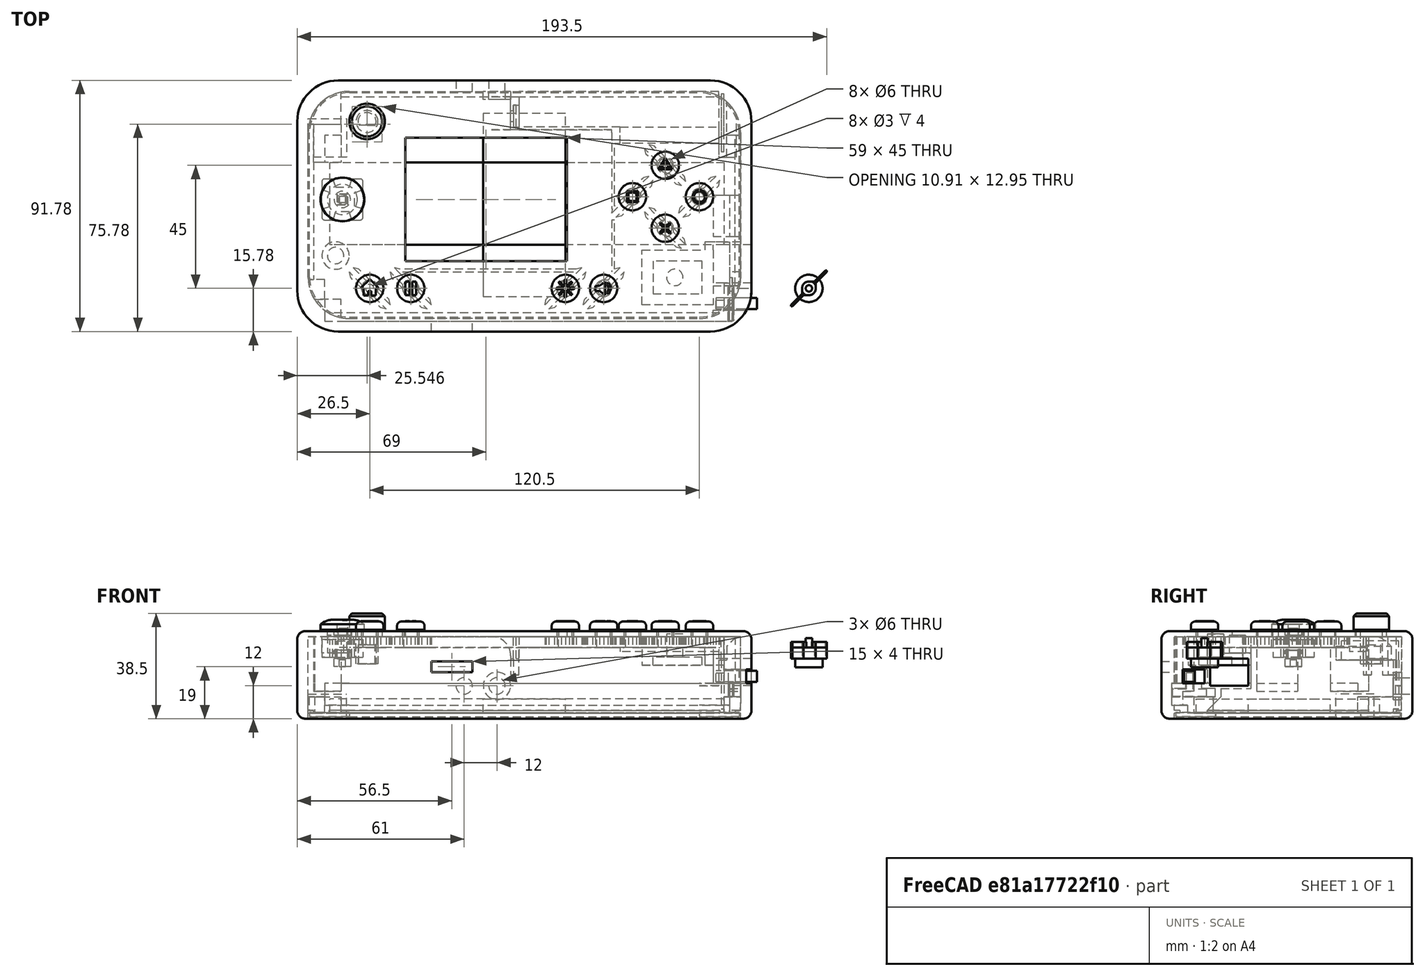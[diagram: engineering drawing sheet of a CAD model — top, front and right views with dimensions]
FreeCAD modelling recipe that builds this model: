
FCSTD DOCUMENT  (FreeCAD 0.18R4 (GitTag))
Label: Master
License: All rights reserved
LicenseURL: http://en.wikipedia.org/wiki/All_rights_reserved
objects: Sketcher::SketchObject×86, PartDesign::Pad×55, PartDesign::Pocket×27, PartDesign::Body×19, PartDesign::FeatureBase×8, PartDesign::Fillet×4, PartDesign::Chamfer×3, PartDesign::ShapeBinder×1, PartDesign::Revolution×1, PartDesign::PolarPattern×1
note: 288 computed .brp shape members not serialized (recipe doc carries the construction recipe); baked Part::Feature solids carry a one-line shape summary decoded from their .brp

FEATURE [Sketcher::SketchObject] Sketch
  MapMode = 5
  Support = -> [XY_Plane]
  sketch-geometry (17):
    g0: GeomPoint X=9e-16 Y=15 Z=0
    g1: GeomPoint X=0 Y=-72.9216 Z=0
    g2: LineSegment StartX=4 StartY=-70.7773 StartZ=0 EndX=140 EndY=-70.7773 EndZ=0
    g3: LineSegment StartX=4 StartY=21 StartZ=0 EndX=140 EndY=21 EndZ=0
    g4: LineSegment StartX=-11 StartY=6 StartZ=0 EndX=-11 EndY=-55.7773 EndZ=0
    g5: ArcOfCircle CenterX=140 CenterY=6 CenterZ=0 NormalX=0 NormalY=0 NormalZ=1 AngleXU=0 Radius=15 StartAngle=0 EndAngle=1.5708
    g6: ArcOfCircle CenterX=140 CenterY=-55.7773 CenterZ=0 NormalX=0 NormalY=0 NormalZ=1 AngleXU=0 Radius=15 StartAngle=4.71239 EndAngle=6.28319
    g7: LineSegment StartX=155 StartY=6 StartZ=0 EndX=155 EndY=-55.7773 EndZ=0
    g8: LineSegment [constr] StartX=140 StartY=21 StartZ=0 EndX=140 EndY=6 EndZ=0
    g9: LineSegment [constr] StartX=140 StartY=6 StartZ=0 EndX=140 EndY=-70.7773 EndZ=0
    g10: LineSegment [constr] StartX=140 StartY=-55.7773 StartZ=0 EndX=155 EndY=-55.7773 EndZ=0
    g11: LineSegment [constr] StartX=155 StartY=6 StartZ=0 EndX=140 EndY=6 EndZ=0
    g12: LineSegment [constr] StartX=4 StartY=21 StartZ=0 EndX=4 EndY=-70.7773 EndZ=0
    g13: ArcOfCircle CenterX=4 CenterY=-55.7773 CenterZ=0 NormalX=0 NormalY=0 NormalZ=1 AngleXU=0 Radius=15 StartAngle=3.14159 EndAngle=4.71239
    g14: LineSegment [constr] StartX=-11 StartY=-55.7773 StartZ=0 EndX=4 EndY=-55.7773 EndZ=0
    g15: LineSegment [constr] StartX=4 StartY=6 StartZ=0 EndX=-11 EndY=6 EndZ=0
    g16: ArcOfCircle CenterX=4 CenterY=6 CenterZ=0 NormalX=0 NormalY=0 NormalZ=1 AngleXU=0 Radius=15 StartAngle=1.5708 EndAngle=3.14159
  constraints (40):
    c: PointOnObject(g1,g-2)
    c: Horizontal(g2)
    c: Horizontal(g3)
    c: Vertical(g4)
    c: Coincident(g5,g3)
    c: Coincident(g6,g2)
    c: Coincident(g7,g5)
    c: Coincident(g7,g6)
    c: Vertical(g7)
    c: Coincident(g8,g3)
    c: Coincident(g8,g5)
    c: Vertical(g8)
    c: Coincident(g9,g5)
    c: Coincident(g9,g2)
    c: Vertical(g9)
    c: PointOnObject(g6,g9)
    c: Distance(g6,g2) = 15
    c: Coincident(g10,g6)
    c: Horizontal(g10)
    c: Coincident(g6,g10)
    c: Coincident(g11,g5)
    c: Coincident(g11,g5)
    c: Vertical(g12)
    c: PointOnObject(g13,g12)
    c: Coincident(g13,g12)
    c: Coincident(g14,g4)
    c: Coincident(g14,g13)
    c: Horizontal(g14)
    c: PointOnObject(g15,g12)
    c: Horizontal(g15)
    c: Coincident(g16,g15)
    c: PointOnObject(g15,g4)
    c: Coincident(g4,g16)
    c: Coincident(g3,g12)
    c: Coincident(g13,g4)
    c: Coincident(g3,g16)
    c: Coincident(g2,g12)
    c: Distance(g13,g2) = 15
    c: Distance(g3,g16) = 15
    c: Horizontal(g11)
FEATURE [PartDesign::Pad] Pad  label="Base"
  Length = 32
  Length2 = 100
  Profile = -> Sketch
  Type = 0
FEATURE [Sketcher::SketchObject] Sketch001
  MapMode = 5
  Placement = pos=(0,0,0) rot=(1,0,0;3.14159rad)
  Support = -> [Pad]
  sketch-geometry (12):
    g0: LineSegment StartX=8 StartY=-17 StartZ=0 EndX=136 EndY=-17 EndZ=0
    g1: LineSegment StartX=151 StartY=51 StartZ=0 EndX=151 EndY=-2 EndZ=0
    g2: LineSegment StartX=8 StartY=66 StartZ=0 EndX=136 EndY=66 EndZ=0
    g3: LineSegment StartX=-7 StartY=51 StartZ=0 EndX=-7 EndY=-2 EndZ=0
    g4: LineSegment [constr] StartX=-7 StartY=-17 StartZ=0 EndX=8 EndY=-2 EndZ=0
    g5: LineSegment [constr] StartX=-7 StartY=66 StartZ=0 EndX=8 EndY=51 EndZ=0
    g6: LineSegment [constr] StartX=151 StartY=66 StartZ=0 EndX=136 EndY=51 EndZ=0
    g7: LineSegment [constr] StartX=151 StartY=-17 StartZ=0 EndX=136 EndY=-2 EndZ=0
    g8: ArcOfCircle CenterX=8 CenterY=51 CenterZ=0 NormalX=0 NormalY=0 NormalZ=1 AngleXU=0 Radius=15 StartAngle=1.5708 EndAngle=3.14159
    g9: ArcOfCircle CenterX=136 CenterY=51 CenterZ=0 NormalX=0 NormalY=0 NormalZ=1 AngleXU=0 Radius=15 StartAngle=0 EndAngle=1.5708
    g10: ArcOfCircle CenterX=136 CenterY=-2 CenterZ=0 NormalX=0 NormalY=0 NormalZ=1 AngleXU=0 Radius=15 StartAngle=4.71239 EndAngle=6.28319
    g11: ArcOfCircle CenterX=8 CenterY=-2 CenterZ=0 NormalX=0 NormalY=0 NormalZ=1 AngleXU=0 Radius=15 StartAngle=3.14159 EndAngle=4.71239
  constraints (16):
    c: Horizontal(g0)
    c: Vertical(g1)
    c: Horizontal(g2)
    c: Vertical(g3)
    c: Coincident(g8,g5)
    c: Coincident(g9,g6)
    c: Coincident(g10,g7)
    c: Coincident(g11,g4)
    c: Coincident(g11,g3)
    c: Coincident(g11,g0)
    c: Coincident(g8,g2)
    c: Coincident(g8,g3)
    c: Coincident(g9,g1)
    c: Coincident(g9,g2)
    c: Coincident(g1,g10)
    c: Coincident(g0,g10)
FEATURE [Sketcher::SketchObject] Sketch002
  MapMode = 5
  Placement = pos=(0,0,32) rot=(0,0,1;0rad)
  Support = -> [Pad]
  sketch-geometry (30):
    g0: LineSegment [constr] StartX=0 StartY=0 StartZ=0 EndX=146 EndY=0 EndZ=0
    g1: LineSegment [constr] StartX=146 StartY=0 StartZ=0 EndX=146 EndY=-66 EndZ=0
    g2: LineSegment [constr] StartX=146 StartY=-66 StartZ=0 EndX=0 EndY=-66 EndZ=0
    g3: LineSegment [constr] StartX=0 StartY=-66 StartZ=0 EndX=0 EndY=0 EndZ=0
    g4: LineSegment [constr] StartX=15.5 StartY=-55 StartZ=0 EndX=101 EndY=-55 EndZ=0
    g5: GeomPoint X=30.5 Y=-55 Z=0
    g6: GeomPoint X=87 Y=-55 Z=0
    g7: LineSegment [constr] StartX=136 StartY=-21.5 StartZ=0 EndX=111.5 EndY=-21.5 EndZ=0
    g8: LineSegment [constr] StartX=123.5 StartY=-10 StartZ=0 EndX=123.5 EndY=-33 EndZ=0
    g9: LineSegment [constr] StartX=26 StartY=2.5 StartZ=0 EndX=94.5 EndY=2.5 EndZ=0
    g10: LineSegment [constr] StartX=94.5 StartY=2.5 StartZ=0 EndX=94.5 EndY=-47.5 EndZ=0
    g11: LineSegment [constr] StartX=94.5 StartY=-47.5 StartZ=0 EndX=26 EndY=-47.5 EndZ=0
    g12: LineSegment [constr] StartX=26 StartY=-47.5 StartZ=0 EndX=26 EndY=2.5 EndZ=0
    g13: GeomPoint X=5.5 Y=-22.5 Z=0
    g14: GeomPoint X=14.5 Y=4 Z=0
    g15: GeomPoint X=6 Y=-46 Z=0
    g16: Circle CenterX=15.5 CenterY=-55 CenterZ=0 NormalX=0 NormalY=0 NormalZ=1 AngleXU=0 Radius=3
    g17: Circle CenterX=30.5 CenterY=-55 CenterZ=0 NormalX=0 NormalY=0 NormalZ=1 AngleXU=0 Radius=3
    g18: Circle CenterX=87 CenterY=-55 CenterZ=0 NormalX=0 NormalY=0 NormalZ=1 AngleXU=0 Radius=3
    g19: Circle CenterX=101 CenterY=-55 CenterZ=0 NormalX=0 NormalY=0 NormalZ=1 AngleXU=0 Radius=3
    g20: Circle CenterX=111.5 CenterY=-21.5 CenterZ=0 NormalX=0 NormalY=0 NormalZ=1 AngleXU=0 Radius=3
    g21: Circle CenterX=136 CenterY=-21.5 CenterZ=0 NormalX=0 NormalY=0 NormalZ=1 AngleXU=0 Radius=3
    g22: Circle CenterX=123.5 CenterY=-33 CenterZ=0 NormalX=0 NormalY=0 NormalZ=1 AngleXU=0 Radius=3
    g23: Circle CenterX=123.5 CenterY=-10 CenterZ=0 NormalX=0 NormalY=0 NormalZ=1 AngleXU=0 Radius=3
    g24: LineSegment StartX=28.5 StartY=0 StartZ=0 EndX=87.5 EndY=0 EndZ=0
    g25: LineSegment StartX=87.5 StartY=0 StartZ=0 EndX=87.5 EndY=-45 EndZ=0
    g26: LineSegment StartX=87.5 StartY=-45 StartZ=0 EndX=28.5 EndY=-45 EndZ=0
    g27: LineSegment StartX=28.5 StartY=-45 StartZ=0 EndX=28.5 EndY=0 EndZ=0
    g28: Circle CenterX=5.5 CenterY=-22.5 CenterZ=0 NormalX=0 NormalY=0 NormalZ=1 AngleXU=0 Radius=5.5
    g29: Circle CenterX=14.5 CenterY=4 CenterZ=0 NormalX=0 NormalY=0 NormalZ=1 AngleXU=0 Radius=5.5
  constraints (63):
    c: Coincident(g0,g1)
    c: Coincident(g1,g2)
    c: Coincident(g2,g3)
    c: Coincident(g3,g0)
    c: Horizontal(g0)
    c: Horizontal(g2)
    c: Vertical(g1)
    c: Vertical(g3)
    c: Coincident(g0,g-1)
    c: Horizontal(g4)
    c: Distance(g3) = 66
    c: Distance(g0) = 146
    c: Distance(g4,g2) = 11
    c: Distance(g4,g3) = 15.5
    c: Distance(g4,g1) = 45
    c: PointOnObject(g5,g4)
    c: Distance(g4,g5) = 15
    c: PointOnObject(g6,g4)
    c: Distance(g6,g4) = 14
    c: Horizontal(g7)
    c: Vertical(g8)
    c: Distance(g7,g0) = 21.5
    c: Distance(g8,g1) = 22.5
    c: Distance(g8,g0) = 10
    c: Distance(g7,g1) = 10
    c: Distance(g8) = 23
    c: Distance(g7) = 24.5
    c: Coincident(g9,g10)
    c: Coincident(g10,g11)
    c: Coincident(g11,g12)
    c: Coincident(g12,g9)
    c: Horizontal(g9)
    c: Horizontal(g11)
    c: Vertical(g10)
    c: Vertical(g12)
    c: Distance(g12) = 50
    c: Distance(g11) = 68.5
    c: Distance(g9,g0) = 2.5
    c: Distance(g9,g3) = 26
    c: Distance(g13,g3) = 5.5
    c: Distance(g13,g0) = 22.5
    c: Distance(g14,g0) = 4
    c: Distance(g14,g3) = 14.5
    c: Distance(g15,g3) = 6
    c: Distance(g15,g2) = 20
    c: Coincident(g16,g4)
    c: Coincident(g17,g5)
    c: Coincident(g18,g6)
    c: Coincident(g19,g4)
    c: Coincident(g20,g7)
    c: Coincident(g22,g8)
    c: Coincident(g23,g8)
    c: Coincident(g24,g25)
    c: Coincident(g25,g26)
    c: Coincident(g26,g27)
    c: Coincident(g27,g24)
    c: Horizontal(g24)
    c: Horizontal(g26)
    c: Vertical(g25)
    c: Vertical(g27)
    c: Distance(g25,g10) = 7
    c: Coincident(g28,g13)
    c: Coincident(g29,g14)
FEATURE [Sketcher::SketchObject] Sketch003  label="Diagram"
  AttachmentOffset = pos=(0,0,-3) rot=(0,0,1;0rad)
  MapMode = 5
  Placement = pos=(0,0,29) rot=(0,0,1;0rad)
  Support = -> [Pad]
  sketch-geometry (34):
    g0: LineSegment StartX=0 StartY=0 StartZ=0 EndX=146 EndY=0 EndZ=0
    g1: LineSegment StartX=146 StartY=0 StartZ=0 EndX=146 EndY=-66 EndZ=0
    g2: LineSegment StartX=146 StartY=-66 StartZ=0 EndX=0 EndY=-66 EndZ=0
    g3: LineSegment StartX=0 StartY=-66 StartZ=0 EndX=0 EndY=0 EndZ=0
    g4: LineSegment [constr] StartX=15.5 StartY=-55 StartZ=0 EndX=101 EndY=-55 EndZ=0
    g5: GeomPoint X=30.5 Y=-55 Z=0
    g6: GeomPoint X=87 Y=-55 Z=0
    g7: LineSegment [constr] StartX=136 StartY=-21.5 StartZ=0 EndX=111.5 EndY=-21.5 EndZ=0
    g8: LineSegment [constr] StartX=123.5 StartY=-10 StartZ=0 EndX=123.5 EndY=-33 EndZ=0
    g9: LineSegment [constr] StartX=26 StartY=2.5 StartZ=0 EndX=94.5 EndY=2.5 EndZ=0
    g10: LineSegment [constr] StartX=94.5 StartY=2.5 StartZ=0 EndX=94.5 EndY=-47.5 EndZ=0
    g11: LineSegment [constr] StartX=94.5 StartY=-47.5 StartZ=0 EndX=26 EndY=-47.5 EndZ=0
    g12: LineSegment [constr] StartX=26 StartY=-47.5 StartZ=0 EndX=26 EndY=2.5 EndZ=0
    g13: GeomPoint X=5.5 Y=-22.5 Z=0
    g14: GeomPoint X=14.5 Y=4 Z=0
    g15: GeomPoint X=6 Y=-46 Z=0
    g16: Circle CenterX=15.5 CenterY=-55 CenterZ=0 NormalX=0 NormalY=0 NormalZ=1 AngleXU=0 Radius=3
    g17: Circle CenterX=30.5 CenterY=-55 CenterZ=0 NormalX=0 NormalY=0 NormalZ=1 AngleXU=0 Radius=3
    g18: Circle CenterX=87 CenterY=-55 CenterZ=0 NormalX=0 NormalY=0 NormalZ=1 AngleXU=0 Radius=3
    g19: Circle CenterX=101 CenterY=-55 CenterZ=0 NormalX=0 NormalY=0 NormalZ=1 AngleXU=0 Radius=3
    g20: Circle CenterX=111.5 CenterY=-21.5 CenterZ=0 NormalX=0 NormalY=0 NormalZ=1 AngleXU=0 Radius=3
    g21: Circle CenterX=136 CenterY=-21.5 CenterZ=0 NormalX=0 NormalY=0 NormalZ=1 AngleXU=0 Radius=3
    g22: Circle CenterX=123.5 CenterY=-33 CenterZ=0 NormalX=0 NormalY=0 NormalZ=1 AngleXU=0 Radius=3
    g23: Circle CenterX=123.5 CenterY=-10 CenterZ=0 NormalX=0 NormalY=0 NormalZ=1 AngleXU=0 Radius=3
    g24: LineSegment StartX=28.5 StartY=0 StartZ=0 EndX=87.5 EndY=0 EndZ=0
    g25: LineSegment StartX=87.5 StartY=0 StartZ=0 EndX=87.5 EndY=-45 EndZ=0
    g26: LineSegment StartX=87.5 StartY=-45 StartZ=0 EndX=28.5 EndY=-45 EndZ=0
    g27: LineSegment StartX=28.5 StartY=-45 StartZ=0 EndX=28.5 EndY=0 EndZ=0
    g28: Circle CenterX=5.5 CenterY=-22.5 CenterZ=0 NormalX=0 NormalY=0 NormalZ=1 AngleXU=0 Radius=3
    g29: Circle CenterX=14.5 CenterY=4 CenterZ=0 NormalX=0 NormalY=0 NormalZ=1 AngleXU=0 Radius=3
    g30: LineSegment StartX=142.166 StartY=-0.619292 StartZ=0 EndX=72.666 EndY=-0.619292 EndZ=0
    g31: LineSegment StartX=72.666 StartY=-0.619292 StartZ=0 EndX=72.666 EndY=17.3807 EndZ=0
    g32: LineSegment StartX=72.666 StartY=17.3807 StartZ=0 EndX=142.166 EndY=17.3807 EndZ=0
    g33: LineSegment StartX=142.166 StartY=17.3807 StartZ=0 EndX=142.166 EndY=-0.619292 EndZ=0
  constraints (72):
    c: Coincident(g0,g1)
    c: Coincident(g1,g2)
    c: Coincident(g2,g3)
    c: Coincident(g3,g0)
    c: Horizontal(g0)
    c: Horizontal(g2)
    c: Vertical(g1)
    c: Vertical(g3)
    c: Coincident(g0,g-1)
    c: Horizontal(g4)
    c: Distance(g3) = 66
    c: Distance(g0) = 146
    c: Distance(g4,g2) = 11
    c: Distance(g4,g3) = 15.5
    c: Distance(g4,g1) = 45
    c: PointOnObject(g5,g4)
    c: Distance(g4,g5) = 15
    c: PointOnObject(g6,g4)
    c: Distance(g6,g4) = 14
    c: Horizontal(g7)
    c: Vertical(g8)
    c: Distance(g7,g0) = 21.5
    c: Distance(g8,g1) = 22.5
    c: Distance(g8,g0) = 10
    c: Distance(g7,g1) = 10
    c: Distance(g8) = 23
    c: Distance(g7) = 24.5
    c: Coincident(g9,g10)
    c: Coincident(g10,g11)
    c: Coincident(g11,g12)
    c: Coincident(g12,g9)
    c: Horizontal(g9)
    c: Horizontal(g11)
    c: Vertical(g10)
    c: Vertical(g12)
    c: Distance(g12) = 50
    c: Distance(g11) = 68.5
    c: Distance(g9,g0) = 2.5
    c: Distance(g9,g3) = 26
    c: Distance(g13,g3) = 5.5
    c: Distance(g13,g0) = 22.5
    c: Distance(g14,g0) = 4
    c: Distance(g14,g3) = 14.5
    c: Distance(g15,g3) = 6
    c: Distance(g15,g2) = 20
    c: Coincident(g16,g4)
    c: Coincident(g17,g5)
    c: Coincident(g18,g6)
    c: Coincident(g19,g4)
    c: Coincident(g20,g7)
    c: Coincident(g22,g8)
    c: Coincident(g23,g8)
    c: Coincident(g24,g25)
    c: Coincident(g25,g26)
    c: Coincident(g26,g27)
    c: Coincident(g27,g24)
    c: Horizontal(g24)
    c: Horizontal(g26)
    c: Vertical(g25)
    c: Vertical(g27)
    c: Distance(g25,g10) = 7
    c: Coincident(g29,g14)
    c: Coincident(g30,g31)
    c: Coincident(g31,g32)
    c: Coincident(g32,g33)
    c: Coincident(g33,g30)
    c: Horizontal(g30)
    c: Horizontal(g32)
    c: Vertical(g31)
    c: Vertical(g33)
    c: Distance(g32) = 69.5
    c: Distance(g33) = 18
FEATURE [PartDesign::Pocket] Pocket  label="Input_holes"
  BaseFeature = -> Pad
  Length = 5
  Length2 = 100
  Profile = -> Sketch002
  Type = 0
FEATURE [PartDesign::Pocket] Pocket001  label="Cutout"
  BaseFeature = -> Pocket
  Length = 30
  Length2 = 100
  Profile = -> Sketch001
  Type = 0
FEATURE [Sketcher::SketchObject] Sketch004
  AttachmentOffset = pos=(0,0,17) rot=(0,0,1;0rad)
  MapMode = 5
  Placement = pos=(0,0,13) rot=(1,0,0;3.14159rad)
  Support = -> [Pocket001]
  sketch-geometry (4):
    g0: LineSegment StartX=147 StartY=58 StartZ=0 EndX=-1 EndY=58 EndZ=0
    g1: LineSegment StartX=-1 StartY=58 StartZ=0 EndX=-1 EndY=67 EndZ=0
    g2: LineSegment StartX=-1 StartY=67 StartZ=0 EndX=147 EndY=67 EndZ=0
    g3: LineSegment StartX=147 StartY=67 StartZ=0 EndX=147 EndY=58 EndZ=0
  constraints (8):
    c: Coincident(g0,g1)
    c: Coincident(g1,g2)
    c: Coincident(g2,g3)
    c: Coincident(g3,g0)
    c: Horizontal(g0)
    c: Horizontal(g2)
    c: Vertical(g1)
    c: Vertical(g3)
FEATURE [PartDesign::Pocket] Pocket002  label="PCB rack"
  BaseFeature = -> Pocket001
  Length = 8
  Length2 = 100
  Profile = -> Sketch004
  Reversed = true
  Type = 0
FEATURE [Sketcher::SketchObject] Sketch005
  MapMode = 5
  Placement = pos=(0,0,30) rot=(1,0,0;3.14159rad)
  Support = -> [Pocket002]
  sketch-geometry (16):
    g0: LineSegment StartX=5 StartY=9 StartZ=0 EndX=-5 EndY=9 EndZ=0
    g1: LineSegment StartX=-5 StartY=9 StartZ=0 EndX=-5 EndY=-5 EndZ=0
    g2: LineSegment StartX=-5 StartY=-5 StartZ=0 EndX=5 EndY=-5 EndZ=0
    g3: LineSegment StartX=5 StartY=-5 StartZ=0 EndX=5 EndY=9 EndZ=0
    g4: LineSegment StartX=5 StartY=59 StartZ=0 EndX=-5 EndY=59 EndZ=0
    g5: LineSegment StartX=-5 StartY=59 StartZ=0 EndX=-5 EndY=67 EndZ=0
    g6: LineSegment StartX=-5 StartY=67 StartZ=0 EndX=5 EndY=67 EndZ=0
    g7: LineSegment StartX=5 StartY=67 StartZ=0 EndX=5 EndY=59 EndZ=0
    g8: LineSegment StartX=141 StartY=63 StartZ=0 EndX=150 EndY=63 EndZ=0
    g9: LineSegment StartX=150 StartY=63 StartZ=0 EndX=150 EndY=66 EndZ=0
    g10: LineSegment StartX=150 StartY=66 StartZ=0 EndX=141 EndY=66 EndZ=0
    g11: LineSegment StartX=141 StartY=66 StartZ=0 EndX=141 EndY=63 EndZ=0
    g12: LineSegment StartX=149 StartY=21 StartZ=0 EndX=141 EndY=21 EndZ=0
    g13: LineSegment StartX=141 StartY=21 StartZ=0 EndX=141 EndY=36 EndZ=0
    g14: LineSegment StartX=141 StartY=36 StartZ=0 EndX=149 EndY=36 EndZ=0
    g15: LineSegment StartX=149 StartY=36 StartZ=0 EndX=149 EndY=21 EndZ=0
  constraints (32):
    c: Coincident(g0,g1)
    c: Coincident(g1,g2)
    c: Coincident(g2,g3)
    c: Coincident(g3,g0)
    c: Horizontal(g0)
    c: Horizontal(g2)
    c: Vertical(g1)
    c: Vertical(g3)
    c: Coincident(g4,g5)
    c: Coincident(g5,g6)
    c: Coincident(g6,g7)
    c: Coincident(g7,g4)
    c: Horizontal(g4)
    c: Horizontal(g6)
    c: Vertical(g5)
    c: Vertical(g7)
    c: Coincident(g8,g9)
    c: Coincident(g9,g10)
    c: Coincident(g10,g11)
    c: Coincident(g11,g8)
    c: Horizontal(g8)
    c: Horizontal(g10)
    c: Vertical(g9)
    c: Vertical(g11)
    c: Coincident(g12,g13)
    c: Coincident(g13,g14)
    c: Coincident(g14,g15)
    c: Coincident(g15,g12)
    c: Horizontal(g12)
    c: Horizontal(g14)
    c: Vertical(g13)
    c: Vertical(g15)
FEATURE [PartDesign::Pad] Pad001  label="PCB holders"
  BaseFeature = -> Pocket002
  Length = 17
  Length2 = 100
  Profile = -> Sketch005
  Type = 0
FEATURE [Sketcher::SketchObject] Sketch007
  MapMode = 5
  Placement = pos=(0,0,13) rot=(1,0,0;3.14159rad)
  Support = -> [Pad001]
  sketch-geometry (14):
    g0: LineSegment StartX=5 StartY=-5 StartZ=0 EndX=5 EndY=-1 EndZ=0
    g1: LineSegment StartX=5 StartY=-1 StartZ=0 EndX=-1 EndY=-1 EndZ=0
    g2: LineSegment StartX=-1 StartY=-1 StartZ=0 EndX=-1 EndY=9 EndZ=0
    g3: LineSegment StartX=-1 StartY=9 StartZ=0 EndX=-5 EndY=9 EndZ=0
    g4: LineSegment StartX=-5 StartY=9 StartZ=0 EndX=-5 EndY=-5 EndZ=0
    g5: LineSegment StartX=-5 StartY=-5 StartZ=0 EndX=5 EndY=-5 EndZ=0
    g6: LineSegment StartX=-1 StartY=59 StartZ=0 EndX=-1 EndY=64 EndZ=0
    g7: LineSegment StartX=-1 StartY=64 StartZ=0 EndX=-5 EndY=64 EndZ=0
    g8: LineSegment StartX=-5 StartY=64 StartZ=0 EndX=-5 EndY=59 EndZ=0
    g9: LineSegment StartX=-5 StartY=59 StartZ=0 EndX=-1 EndY=59 EndZ=0
    g10: LineSegment StartX=147 StartY=36 StartZ=0 EndX=151 EndY=36 EndZ=0
    g11: LineSegment StartX=151 StartY=36 StartZ=0 EndX=151 EndY=21 EndZ=0
    g12: LineSegment StartX=151 StartY=21 StartZ=0 EndX=147 EndY=21 EndZ=0
    g13: LineSegment StartX=147 StartY=21 StartZ=0 EndX=147 EndY=36 EndZ=0
  constraints (28):
    c: Vertical(g0)
    c: Coincident(g0,g1)
    c: Horizontal(g1)
    c: Coincident(g1,g2)
    c: Vertical(g2)
    c: Coincident(g2,g3)
    c: Horizontal(g3)
    c: Coincident(g3,g4)
    c: Vertical(g4)
    c: Coincident(g4,g5)
    c: Coincident(g5,g0)
    c: Horizontal(g5)
    c: Vertical(g6)
    c: Coincident(g6,g7)
    c: Horizontal(g7)
    c: Coincident(g7,g8)
    c: Vertical(g8)
    c: Coincident(g8,g9)
    c: Coincident(g9,g6)
    c: Horizontal(g9)
    c: Coincident(g10,g11)
    c: Coincident(g11,g12)
    c: Coincident(g12,g13)
    c: Coincident(g13,g10)
    c: Horizontal(g10)
    c: Horizontal(g12)
    c: Vertical(g11)
    c: Vertical(g13)
FEATURE [PartDesign::Pad] Pad002  label="PCB holder rims"
  BaseFeature = -> Pad001
  Length = 3
  Length2 = 100
  Profile = -> Sketch007
  Type = 0
FEATURE [Sketcher::SketchObject] Sketch008
  MapMode = 5
  Placement = pos=(0,0,30) rot=(1,0,0;3.14159rad)
  Support = -> [Pad002]
  sketch-geometry (4):
    g0: LineSegment StartX=70 StartY=-15 StartZ=0 EndX=143 EndY=-15 EndZ=0
    g1: LineSegment StartX=143 StartY=-15 StartZ=0 EndX=143 EndY=-17 EndZ=0
    g2: LineSegment StartX=143 StartY=-17 StartZ=0 EndX=70 EndY=-17 EndZ=0
    g3: LineSegment StartX=70 StartY=-17 StartZ=0 EndX=70 EndY=-15 EndZ=0
  constraints (8):
    c: Coincident(g0,g1)
    c: Coincident(g1,g2)
    c: Coincident(g2,g3)
    c: Coincident(g3,g0)
    c: Horizontal(g0)
    c: Horizontal(g2)
    c: Vertical(g1)
    c: Vertical(g3)
FEATURE [PartDesign::Pocket] Pocket003  label="Battery cutout"
  BaseFeature = -> Pad002
  Length = 18
  Length2 = 100
  Profile = -> Sketch008
  Reversed = true
  Type = 0
FEATURE [Sketcher::SketchObject] Sketch009
  MapMode = 5
  Placement = pos=(0,0,30) rot=(1,0,0;3.14159rad)
  Support = -> [Pocket003]
  sketch-geometry (4):
    g0: LineSegment StartX=143 StartY=7 StartZ=0 EndX=146 EndY=7 EndZ=0
    g1: LineSegment StartX=146 StartY=7 StartZ=0 EndX=146 EndY=-16 EndZ=0
    g2: LineSegment StartX=146 StartY=-16 StartZ=0 EndX=143 EndY=-16 EndZ=0
    g3: LineSegment StartX=143 StartY=-16 StartZ=0 EndX=143 EndY=7 EndZ=0
  constraints (8):
    c: Coincident(g0,g1)
    c: Coincident(g1,g2)
    c: Coincident(g2,g3)
    c: Coincident(g3,g0)
    c: Horizontal(g0)
    c: Horizontal(g2)
    c: Vertical(g1)
    c: Vertical(g3)
FEATURE [PartDesign::Pad] Pad003  label="Battery holder +"
  BaseFeature = -> Pocket003
  Length = 8.5
  Length2 = 100
  Profile = -> Sketch009
  Type = 0
FEATURE [Sketcher::SketchObject] Sketch010
  MapMode = 5
  Placement = pos=(0,0,21.5) rot=(1,0,0;3.14159rad)
  Support = -> [Pad003]
  sketch-geometry (4):
    g0: LineSegment StartX=144 StartY=5 StartZ=0 EndX=145 EndY=5 EndZ=0
    g1: LineSegment StartX=145 StartY=5 StartZ=0 EndX=145 EndY=-16 EndZ=0
    g2: LineSegment StartX=145 StartY=-16 StartZ=0 EndX=144 EndY=-16 EndZ=0
    g3: LineSegment StartX=144 StartY=-16 StartZ=0 EndX=144 EndY=5 EndZ=0
  constraints (8):
    c: Coincident(g0,g1)
    c: Coincident(g1,g2)
    c: Coincident(g2,g3)
    c: Coincident(g3,g0)
    c: Horizontal(g0)
    c: Horizontal(g2)
    c: Vertical(g1)
    c: Vertical(g3)
FEATURE [PartDesign::Pocket] Pocket004  label="Battery holder (+) cutout"
  BaseFeature = -> Pad003
  Length = 7
  Length2 = 100
  Profile = -> Sketch010
  Type = 0
FEATURE [Sketcher::SketchObject] Sketch011
  MapMode = 5
  Placement = pos=(0,0,21.5) rot=(1,0,0;3.14159rad)
  Support = -> [Pad003]
  sketch-geometry (4):
    g0: LineSegment StartX=144 StartY=5 StartZ=0 EndX=145 EndY=5 EndZ=0
    g1: LineSegment StartX=145 StartY=5 StartZ=0 EndX=145 EndY=-16 EndZ=0
    g2: LineSegment StartX=145 StartY=-16 StartZ=0 EndX=144 EndY=-16 EndZ=0
    g3: LineSegment StartX=144 StartY=-16 StartZ=0 EndX=144 EndY=5 EndZ=0
  constraints (8):
    c: Coincident(g0,g1)
    c: Coincident(g1,g2)
    c: Coincident(g2,g3)
    c: Coincident(g3,g0)
    c: Horizontal(g0)
    c: Horizontal(g2)
    c: Vertical(g1)
    c: Vertical(g3)
FEATURE [PartDesign::Pocket] Pocket005  label="Battery holder (+) up cutout"
  BaseFeature = -> Pocket004
  Length = 18
  Length2 = 100
  Profile = -> Sketch011
  Reversed = true
  Type = 0
FEATURE [Sketcher::SketchObject] Sketch012
  MapMode = 5
  Placement = pos=(0,0,30) rot=(1,0,0;3.14159rad)
  Support = -> [Pocket005]
  sketch-geometry (4):
    g0: LineSegment StartX=70 StartY=-2 StartZ=0 EndX=67 EndY=-2 EndZ=0
    g1: LineSegment StartX=67 StartY=-2 StartZ=0 EndX=67 EndY=-15 EndZ=0
    g2: LineSegment StartX=67 StartY=-15 StartZ=0 EndX=70 EndY=-15 EndZ=0
    g3: LineSegment StartX=70 StartY=-15 StartZ=0 EndX=70 EndY=-2 EndZ=0
  constraints (8):
    c: Coincident(g0,g1)
    c: Coincident(g1,g2)
    c: Coincident(g2,g3)
    c: Coincident(g3,g0)
    c: Horizontal(g0)
    c: Horizontal(g2)
    c: Vertical(g1)
    c: Vertical(g3)
FEATURE [PartDesign::Pad] Pad004  label="Battery holder (-)"
  BaseFeature = -> Pocket005
  Length = 8
  Length2 = 100
  Profile = -> Sketch012
  Type = 0
FEATURE [Sketcher::SketchObject] Sketch013
  MapMode = 5
  Placement = pos=(0,0,22) rot=(1,0,0;3.14159rad)
  Support = -> [Pad004]
  sketch-geometry (4):
    g0: LineSegment StartX=69 StartY=-12 StartZ=0 EndX=68 EndY=-12 EndZ=0
    g1: LineSegment StartX=68 StartY=-12 StartZ=0 EndX=68 EndY=-4 EndZ=0
    g2: LineSegment StartX=68 StartY=-4 StartZ=0 EndX=69 EndY=-4 EndZ=0
    g3: LineSegment StartX=69 StartY=-4 StartZ=0 EndX=69 EndY=-12 EndZ=0
  constraints (8):
    c: Coincident(g0,g1)
    c: Coincident(g1,g2)
    c: Coincident(g2,g3)
    c: Coincident(g3,g0)
    c: Horizontal(g0)
    c: Horizontal(g2)
    c: Vertical(g1)
    c: Vertical(g3)
FEATURE [PartDesign::Pocket] Pocket006  label="Battery holder (-) cutout"
  BaseFeature = -> Pad004
  Length = 8
  Length2 = 100
  Profile = -> Sketch013
  Type = 0
FEATURE [Sketcher::SketchObject] Sketch014
  MapMode = 5
  Placement = pos=(0,0,30) rot=(1,0,0;3.14159rad)
  Support = -> [Pocket006]
  sketch-geometry (143):
    g0: LineSegment [constr] StartX=58.75 StartY=60 StartZ=0 EndX=58.75 EndY=48.75 EndZ=0
    g1: LineSegment [constr] StartX=15.5 StartY=55 StartZ=0 EndX=72 EndY=55 EndZ=0
    g2: LineSegment [constr] StartX=101 StartY=55 StartZ=0 EndX=94.5 EndY=61.5 EndZ=0
    g3: LineSegment [constr] StartX=101 StartY=55 StartZ=0 EndX=107.5 EndY=48.5 EndZ=0
    g4: LineSegment [constr] StartX=136 StartY=21.5 StartZ=0 EndX=129.5 EndY=28 EndZ=0
    g5: LineSegment [constr] StartX=136 StartY=21.5 StartZ=0 EndX=142.5 EndY=15 EndZ=0
    g6: LineSegment [constr] StartX=123.5 StartY=10 StartZ=0 EndX=117 EndY=3.5 EndZ=0
    g7: LineSegment [constr] StartX=123.5 StartY=10 StartZ=0 EndX=130 EndY=16.5 EndZ=0
    g8: LineSegment [constr] StartX=111.5 StartY=21.5 StartZ=0 EndX=118 EndY=15 EndZ=0
    g9: LineSegment [constr] StartX=111.5 StartY=21.5 StartZ=0 EndX=105 EndY=28 EndZ=0
    g10: LineSegment StartX=123.5 StartY=7 StartZ=0 EndX=119.5 EndY=3 EndZ=0
    g11: LineSegment StartX=117.5 StartY=2.5 StartZ=0 EndX=122 EndY=7 EndZ=0
    g12: LineSegment StartX=122 StartY=7 StartZ=0 EndX=123.5 EndY=7 EndZ=0
    g13: LineSegment StartX=120.5 StartY=8.5 StartZ=0 EndX=120.5 EndY=10 EndZ=0
    g14: LineSegment StartX=120.5 StartY=8.5 StartZ=0 EndX=116 EndY=4 EndZ=0
    g15: LineSegment StartX=120.5 StartY=10 StartZ=0 EndX=116.5 EndY=6 EndZ=0
    g16: LineSegment StartX=126.5 StartY=10 StartZ=0 EndX=130.5 EndY=14 EndZ=0
    g17: LineSegment StartX=131 StartY=16 StartZ=0 EndX=126.5 EndY=11.5 EndZ=0
    g18: LineSegment StartX=126.5 StartY=11.5 StartZ=0 EndX=126.5 EndY=10 EndZ=0
    g19: LineSegment StartX=123.5 StartY=13 StartZ=0 EndX=125 EndY=13 EndZ=0
    g20: LineSegment StartX=125 StartY=13 StartZ=0 EndX=129.5 EndY=17.5 EndZ=0
    g21: LineSegment StartX=123.5 StartY=13 StartZ=0 EndX=127.5 EndY=17 EndZ=0
    g22: LineSegment StartX=119.5 StartY=3 StartZ=0 EndX=117.5 EndY=2.5 EndZ=0
    g23: LineSegment StartX=116.5 StartY=6 StartZ=0 EndX=116 EndY=4 EndZ=0
    g24: LineSegment StartX=129.5 StartY=17.5 StartZ=0 EndX=127.5 EndY=17 EndZ=0
    g25: LineSegment StartX=131 StartY=16 StartZ=0 EndX=130.5 EndY=14 EndZ=0
    g26: LineSegment StartX=129.5 StartY=40.5 StartZ=0 EndX=127.5 EndY=40 EndZ=0
    g27: LineSegment StartX=131 StartY=39 StartZ=0 EndX=130.5 EndY=37 EndZ=0
    g28: LineSegment StartX=126.5 StartY=33 StartZ=0 EndX=130.5 EndY=37 EndZ=0
    g29: LineSegment StartX=131 StartY=39 StartZ=0 EndX=126.5 EndY=34.5 EndZ=0
    g30: LineSegment StartX=126.5 StartY=34.5 StartZ=0 EndX=126.5 EndY=33 EndZ=0
    g31: LineSegment StartX=125 StartY=36 StartZ=0 EndX=129.5 EndY=40.5 EndZ=0
    g32: LineSegment StartX=123.5 StartY=36 StartZ=0 EndX=125 EndY=36 EndZ=0
    g33: LineSegment StartX=123.5 StartY=36 StartZ=0 EndX=127.5 EndY=40 EndZ=0
    g34: LineSegment StartX=123.5 StartY=30 StartZ=0 EndX=119.5 EndY=26 EndZ=0
    g35: LineSegment StartX=117.5 StartY=25.5 StartZ=0 EndX=122 EndY=30 EndZ=0
    g36: LineSegment StartX=122 StartY=30 StartZ=0 EndX=123.5 EndY=30 EndZ=0
    g37: LineSegment StartX=120.5 StartY=31.5 StartZ=0 EndX=120.5 EndY=33 EndZ=0
    g38: LineSegment StartX=120.5 StartY=31.5 StartZ=0 EndX=116 EndY=27 EndZ=0
    g39: LineSegment StartX=120.5 StartY=33 StartZ=0 EndX=116.5 EndY=29 EndZ=0
    g40: LineSegment StartX=119.5 StartY=26 StartZ=0 EndX=117.5 EndY=25.5 EndZ=0
    g41: LineSegment StartX=116.5 StartY=29 StartZ=0 EndX=116 EndY=27 EndZ=0
    g42: LineSegment [constr] StartX=117 StartY=26.5 StartZ=0 EndX=130 EndY=39.5 EndZ=0
    g43: LineSegment StartX=108.5 StartY=21.5 StartZ=0 EndX=104.5 EndY=25.5 EndZ=0
    g44: LineSegment StartX=111.5 StartY=24.5 StartZ=0 EndX=107.5 EndY=28.5 EndZ=0
    g45: LineSegment StartX=104 StartY=27.5 StartZ=0 EndX=108.5 EndY=23 EndZ=0
    g46: LineSegment StartX=108.5 StartY=23 StartZ=0 EndX=108.5 EndY=21.5 EndZ=0
    g47: LineSegment StartX=111.5 StartY=24.5 StartZ=0 EndX=110 EndY=24.5 EndZ=0
    g48: LineSegment StartX=110 StartY=24.5 StartZ=0 EndX=105.5 EndY=29 EndZ=0
    g49: LineSegment StartX=111.5 StartY=18.5 StartZ=0 EndX=115.5 EndY=14.5 EndZ=0
    g50: LineSegment StartX=117.5 StartY=14 StartZ=0 EndX=113 EndY=18.5 EndZ=0
    g51: LineSegment StartX=113 StartY=18.5 StartZ=0 EndX=111.5 EndY=18.5 EndZ=0
    g52: LineSegment StartX=114.5 StartY=20 StartZ=0 EndX=114.5 EndY=21.5 EndZ=0
    g53: LineSegment StartX=114.5 StartY=21.5 StartZ=0 EndX=118.5 EndY=17.5 EndZ=0
    g54: LineSegment StartX=114.5 StartY=20 StartZ=0 EndX=119 EndY=15.5 EndZ=0
    g55: LineSegment StartX=107.5 StartY=28.5 StartZ=0 EndX=105.5 EndY=29 EndZ=0
    g56: LineSegment StartX=104 StartY=27.5 StartZ=0 EndX=104.5 EndY=25.5 EndZ=0
    g57: LineSegment StartX=118.5 StartY=17.5 StartZ=0 EndX=119 EndY=15.5 EndZ=0
    g58: LineSegment StartX=117.5 StartY=14 StartZ=0 EndX=115.5 EndY=14.5 EndZ=0
    g59: LineSegment [constr] StartX=136 StartY=21.5 StartZ=0 EndX=129.5 EndY=28 EndZ=0
    g60: LineSegment StartX=133 StartY=21.5 StartZ=0 EndX=129 EndY=25.5 EndZ=0
    g61: LineSegment StartX=136 StartY=24.5 StartZ=0 EndX=132 EndY=28.5 EndZ=0
    g62: LineSegment StartX=128.5 StartY=27.5 StartZ=0 EndX=133 EndY=23 EndZ=0
    g63: LineSegment StartX=133 StartY=23 StartZ=0 EndX=133 EndY=21.5 EndZ=0
    g64: LineSegment StartX=136 StartY=24.5 StartZ=0 EndX=134.5 EndY=24.5 EndZ=0
    g65: LineSegment StartX=134.5 StartY=24.5 StartZ=0 EndX=130 EndY=29 EndZ=0
    g66: LineSegment StartX=132 StartY=28.5 StartZ=0 EndX=130 EndY=29 EndZ=0
    g67: LineSegment StartX=128.5 StartY=27.5 StartZ=0 EndX=129 EndY=25.5 EndZ=0
    g68: LineSegment [constr] StartX=136 StartY=21.5 StartZ=0 EndX=142.5 EndY=15 EndZ=0
    g69: LineSegment StartX=136 StartY=18.5 StartZ=0 EndX=140 EndY=14.5 EndZ=0
    g70: LineSegment StartX=142 StartY=14 StartZ=0 EndX=137.5 EndY=18.5 EndZ=0
    g71: LineSegment StartX=137.5 StartY=18.5 StartZ=0 EndX=136 EndY=18.5 EndZ=0
    g72: LineSegment StartX=139 StartY=20 StartZ=0 EndX=139 EndY=21.5 EndZ=0
    g73: LineSegment StartX=139 StartY=21.5 StartZ=0 EndX=143 EndY=17.5 EndZ=0
    g74: LineSegment StartX=139 StartY=20 StartZ=0 EndX=143.5 EndY=15.5 EndZ=0
    g75: LineSegment StartX=143 StartY=17.5 StartZ=0 EndX=143.5 EndY=15.5 EndZ=0
    g76: LineSegment StartX=142 StartY=14 StartZ=0 EndX=140 EndY=14.5 EndZ=0
    g77: LineSegment StartX=98 StartY=55 StartZ=0 EndX=94 EndY=59 EndZ=0
    g78: LineSegment StartX=101 StartY=58 StartZ=0 EndX=97 EndY=62 EndZ=0
    g79: LineSegment StartX=93.5 StartY=61 StartZ=0 EndX=98 EndY=56.5 EndZ=0
    g80: LineSegment StartX=98 StartY=56.5 StartZ=0 EndX=98 EndY=55 EndZ=0
    g81: LineSegment StartX=101 StartY=58 StartZ=0 EndX=99.5 EndY=58 EndZ=0
    g82: LineSegment StartX=99.5 StartY=58 StartZ=0 EndX=95 EndY=62.5 EndZ=0
    g83: LineSegment StartX=102.5 StartY=52 StartZ=0 EndX=101 EndY=52 EndZ=0
    g84: LineSegment StartX=104 StartY=53.5 StartZ=0 EndX=104 EndY=55 EndZ=0
    g85: LineSegment StartX=97 StartY=62 StartZ=0 EndX=95 EndY=62.5 EndZ=0
    g86: LineSegment StartX=93.5 StartY=61 StartZ=0 EndX=94 EndY=59 EndZ=0
    g87: LineSegment StartX=101 StartY=52 StartZ=0 EndX=105 EndY=48 EndZ=0
    g88: LineSegment StartX=107 StartY=47.5 StartZ=0 EndX=102.5 EndY=52 EndZ=0
    g89: LineSegment StartX=104 StartY=55 StartZ=0 EndX=108 EndY=51 EndZ=0
    g90: LineSegment StartX=104 StartY=53.5 StartZ=0 EndX=108.5 EndY=49 EndZ=0
    g91: LineSegment StartX=108 StartY=51 StartZ=0 EndX=108.5 EndY=49 EndZ=0
    g92: LineSegment StartX=107 StartY=47.5 StartZ=0 EndX=105 EndY=48 EndZ=0
    g93: LineSegment [constr] StartX=87 StartY=55 StartZ=0 EndX=93.5 EndY=48.5 EndZ=0
    g94: LineSegment StartX=90 StartY=53.5 StartZ=0 EndX=90 EndY=55 EndZ=0
    g95: LineSegment StartX=87 StartY=52 StartZ=0 EndX=91 EndY=48 EndZ=0
    g96: LineSegment StartX=93 StartY=47.5 StartZ=0 EndX=88.5 EndY=52 EndZ=0
    g97: LineSegment StartX=90 StartY=55 StartZ=0 EndX=94 EndY=51 EndZ=0
    g98: LineSegment StartX=90 StartY=53.5 StartZ=0 EndX=94.5 EndY=49 EndZ=0
    g99: LineSegment StartX=94 StartY=51 StartZ=0 EndX=94.5 EndY=49 EndZ=0
    g100: LineSegment StartX=93 StartY=47.5 StartZ=0 EndX=91 EndY=48 EndZ=0
    g101: LineSegment StartX=88.5 StartY=52 StartZ=0 EndX=87 EndY=52 EndZ=0
    g102: LineSegment StartX=87 StartY=58 StartZ=0 EndX=83 EndY=62 EndZ=0
    g103: LineSegment StartX=79.5 StartY=61 StartZ=0 EndX=84 EndY=56.5 EndZ=0
    g104: LineSegment StartX=87 StartY=58 StartZ=0 EndX=85.5 EndY=58 EndZ=0
    g105: LineSegment StartX=85.5 StartY=58 StartZ=0 EndX=81 EndY=62.5 EndZ=0
    g106: LineSegment StartX=83 StartY=62 StartZ=0 EndX=81 EndY=62.5 EndZ=0
    g107: LineSegment StartX=79.5 StartY=61 StartZ=0 EndX=80 EndY=59 EndZ=0
    g108: LineSegment StartX=84 StartY=55 StartZ=0 EndX=80 EndY=59 EndZ=0
    g109: LineSegment StartX=84 StartY=56.5 StartZ=0 EndX=84 EndY=55 EndZ=0
    g110: LineSegment StartX=15.5 StartY=52 StartZ=0 EndX=11.5 EndY=48 EndZ=0
    g111: LineSegment StartX=9.5 StartY=47.5 StartZ=0 EndX=14 EndY=52 EndZ=0
    g112: LineSegment StartX=14 StartY=52 StartZ=0 EndX=15.5 EndY=52 EndZ=0
    g113: LineSegment StartX=12.5 StartY=53.5 StartZ=0 EndX=8 EndY=49 EndZ=0
    g114: LineSegment StartX=12.5 StartY=55 StartZ=0 EndX=8.5 EndY=51 EndZ=0
    g115: LineSegment StartX=11.5 StartY=48 StartZ=0 EndX=9.5 EndY=47.5 EndZ=0
    g116: LineSegment StartX=8.5 StartY=51 StartZ=0 EndX=8 EndY=49 EndZ=0
    g117: LineSegment StartX=12.5 StartY=53.5 StartZ=0 EndX=12.5 EndY=55 EndZ=0
    g118: LineSegment StartX=15.5 StartY=58 StartZ=0 EndX=17 EndY=58 EndZ=0
    g119: LineSegment StartX=17 StartY=58 StartZ=0 EndX=21.5 EndY=62.5 EndZ=0
    g120: LineSegment StartX=15.5 StartY=58 StartZ=0 EndX=19.5 EndY=62 EndZ=0
    g121: LineSegment StartX=21.5 StartY=62.5 StartZ=0 EndX=19.5 EndY=62 EndZ=0
    g122: LineSegment StartX=18.5 StartY=55 StartZ=0 EndX=22.5 EndY=59 EndZ=0
    g123: LineSegment StartX=23 StartY=61 StartZ=0 EndX=18.5 EndY=56.5 EndZ=0
    g124: LineSegment StartX=18.5 StartY=56.5 StartZ=0 EndX=18.5 EndY=55 EndZ=0
    g125: LineSegment StartX=23 StartY=61 StartZ=0 EndX=22.5 EndY=59 EndZ=0
    g126: LineSegment StartX=30.5 StartY=58 StartZ=0 EndX=32 EndY=58 EndZ=0
    g127: LineSegment StartX=32 StartY=58 StartZ=0 EndX=36.5 EndY=62.5 EndZ=0
    g128: LineSegment StartX=30.5 StartY=58 StartZ=0 EndX=34.5 EndY=62 EndZ=0
    g129: LineSegment StartX=36.5 StartY=62.5 StartZ=0 EndX=34.5 EndY=62 EndZ=0
    g130: LineSegment StartX=38 StartY=61 StartZ=0 EndX=37.5 EndY=59 EndZ=0
    g131: LineSegment StartX=33.5 StartY=55 StartZ=0 EndX=37.5 EndY=59 EndZ=0
    g132: LineSegment StartX=38 StartY=61 StartZ=0 EndX=33.5 EndY=56.5 EndZ=0
    g133: LineSegment StartX=33.5 StartY=56.5 StartZ=0 EndX=33.5 EndY=55 EndZ=0
    g134: LineSegment StartX=27.5 StartY=53.5 StartZ=0 EndX=23 EndY=49 EndZ=0
    g135: LineSegment StartX=27.5 StartY=55 StartZ=0 EndX=23.5 EndY=51 EndZ=0
    g136: LineSegment StartX=26.5 StartY=48 StartZ=0 EndX=24.5 EndY=47.5 EndZ=0
    g137: LineSegment StartX=23.5 StartY=51 StartZ=0 EndX=23 EndY=49 EndZ=0
    g138: LineSegment StartX=27.5 StartY=53.5 StartZ=0 EndX=27.5 EndY=55 EndZ=0
    g139: LineSegment StartX=30.5 StartY=52 StartZ=0 EndX=26.5 EndY=48 EndZ=0
    g140: LineSegment StartX=24.5 StartY=47.5 StartZ=0 EndX=29 EndY=52 EndZ=0
    g141: LineSegment StartX=29 StartY=52 StartZ=0 EndX=30.5 EndY=52 EndZ=0
    g142: LineSegment [constr] StartX=87 StartY=55 StartZ=0 EndX=80.5 EndY=61.5 EndZ=0
  constraints (167):
    c: Vertical(g0)
    c: Horizontal(g1)
    c: Coincident(g7,g6)
    c: Coincident(g9,g8)
    c: Coincident(g17,g18)
    c: Coincident(g18,g16)
    c: Vertical(g18)
    c: Coincident(g21,g19)
    c: Horizontal(g19)
    c: Coincident(g19,g20)
    c: Coincident(g11,g12)
    c: Coincident(g12,g10)
    c: Horizontal(g12)
    c: Coincident(g13,g15)
    c: Vertical(g13)
    c: Coincident(g13,g14)
    c: Coincident(g21,g7)
    c: Coincident(g22,g10)
    c: Coincident(g22,g11)
    c: Coincident(g23,g15)
    c: Coincident(g23,g14)
    c: Coincident(g24,g20)
    c: Coincident(g24,g21)
    c: Coincident(g25,g17)
    c: Coincident(g25,g16)
    c: Coincident(g29,g30)
    c: Coincident(g30,g28)
    c: Vertical(g30)
    c: Coincident(g33,g32)
    c: Horizontal(g32)
    c: Coincident(g32,g31)
    c: Coincident(g35,g36)
    c: Coincident(g36,g34)
    c: Horizontal(g36)
    c: Coincident(g37,g39)
    c: Vertical(g37)
    c: Coincident(g37,g38)
    c: Coincident(g40,g34)
    c: Coincident(g40,g35)
    c: Coincident(g41,g39)
    c: Coincident(g41,g38)
    c: Coincident(g26,g31)
    c: Coincident(g26,g33)
    c: Coincident(g27,g29)
    c: Coincident(g27,g28)
    c: Coincident(g45,g46)
    c: Coincident(g46,g43)
    c: Vertical(g46)
    c: Coincident(g44,g47)
    c: Horizontal(g47)
    c: Coincident(g47,g48)
    c: Coincident(g50,g51)
    c: Coincident(g51,g49)
    c: Horizontal(g51)
    c: Coincident(g52,g53)
    c: Vertical(g52)
    c: Coincident(g52,g54)
    c: Coincident(g55,g44)
    c: Coincident(g55,g48)
    c: Coincident(g56,g45)
    c: Coincident(g56,g43)
    c: Coincident(g57,g53)
    c: Coincident(g57,g54)
    c: Coincident(g58,g50)
    c: Coincident(g58,g49)
    c: Coincident(g59,g68)
    c: Coincident(g62,g63)
    c: Coincident(g63,g60)
    c: Vertical(g63)
    c: Coincident(g61,g64)
    c: Horizontal(g64)
    c: Coincident(g64,g65)
    c: Coincident(g70,g71)
    c: Coincident(g71,g69)
    c: Horizontal(g71)
    c: Coincident(g72,g73)
    c: Vertical(g72)
    c: Coincident(g72,g74)
    c: Coincident(g66,g61)
    c: Coincident(g66,g65)
    c: Coincident(g67,g62)
    c: Coincident(g67,g60)
    c: Coincident(g75,g73)
    c: Coincident(g75,g74)
    c: Coincident(g76,g70)
    c: Coincident(g76,g69)
    c: Coincident(g79,g80)
    c: Coincident(g80,g77)
    c: Vertical(g80)
    c: Coincident(g78,g81)
    c: Horizontal(g81)
    c: Coincident(g81,g82)
    c: Coincident(g88,g83)
    c: Coincident(g83,g87)
    c: Horizontal(g83)
    c: Coincident(g84,g89)
    c: Vertical(g84)
    c: Coincident(g84,g90)
    c: Coincident(g85,g78)
    c: Coincident(g85,g82)
    c: Coincident(g86,g79)
    c: Coincident(g86,g77)
    c: Coincident(g91,g89)
    c: Coincident(g91,g90)
    c: Coincident(g92,g88)
    c: Coincident(g92,g87)
    c: Coincident(g103,g109)
    c: Coincident(g109,g108)
    c: Vertical(g109)
    c: Coincident(g102,g104)
    c: Horizontal(g104)
    c: Coincident(g104,g105)
    c: Coincident(g96,g101)
    c: Coincident(g101,g95)
    c: Horizontal(g101)
    c: Coincident(g94,g97)
    c: Vertical(g94)
    c: Coincident(g94,g98)
    c: Coincident(g106,g102)
    c: Coincident(g106,g105)
    c: Coincident(g107,g103)
    c: Coincident(g107,g108)
    c: Coincident(g99,g97)
    c: Coincident(g99,g98)
    c: Coincident(g100,g96)
    c: Coincident(g100,g95)
    c: Coincident(g123,g124)
    c: Coincident(g124,g122)
    c: Vertical(g124)
    c: Coincident(g120,g118)
    c: Horizontal(g118)
    c: Coincident(g118,g119)
    c: Coincident(g111,g112)
    c: Coincident(g112,g110)
    c: Horizontal(g112)
    c: Coincident(g117,g114)
    c: Vertical(g117)
    c: Coincident(g117,g113)
    c: Coincident(g115,g110)
    c: Coincident(g115,g111)
    c: Coincident(g116,g114)
    c: Coincident(g116,g113)
    c: Coincident(g121,g119)
    c: Coincident(g121,g120)
    c: Coincident(g125,g123)
    c: Coincident(g125,g122)
    c: Coincident(g132,g133)
    c: Coincident(g133,g131)
    c: Vertical(g133)
    c: Coincident(g128,g126)
    c: Horizontal(g126)
    c: Coincident(g126,g127)
    c: Coincident(g140,g141)
    c: Coincident(g141,g139)
    c: Horizontal(g141)
    c: Coincident(g138,g135)
    c: Vertical(g138)
    c: Coincident(g138,g134)
    c: Coincident(g136,g139)
    c: Coincident(g136,g140)
    c: Coincident(g137,g135)
    c: Coincident(g137,g134)
    c: Coincident(g129,g127)
    c: Coincident(g129,g128)
    c: Coincident(g130,g132)
    c: Coincident(g130,g131)
    c: Coincident(g142,g93)
FEATURE [PartDesign::Pad] Pad005  label="Button stabilizers"
  BaseFeature = -> Pocket006
  Length = 4
  Length2 = 100
  Profile = -> Sketch014
  Type = 0
FEATURE [Sketcher::SketchObject] Sketch016
  MapMode = 5
  Placement = pos=(0,0,30) rot=(1,0,0;3.14159rad)
  sketch-geometry (1):
    g0: Circle CenterX=3 CenterY=43 CenterZ=0 NormalX=0 NormalY=0 NormalZ=1 AngleXU=0 Radius=5
FEATURE [PartDesign::Pad] Pad006  label="control LED"
  BaseFeature = -> Pad005
  Length = 6
  Length2 = 100
  Profile = -> Sketch016
  Type = 0
FEATURE [Sketcher::SketchObject] Sketch017
  MapMode = 5
  Placement = pos=(0,0,24) rot=(1,0,0;3.14159rad)
  Support = -> [Pad006]
  sketch-geometry (1):
    g0: Circle CenterX=3 CenterY=43 CenterZ=0 NormalX=0 NormalY=0 NormalZ=1 AngleXU=0 Radius=3
FEATURE [Sketcher::SketchObject] Sketch018
  MapMode = 5
  Placement = pos=(0,0,30) rot=(1,0,0;3.14159rad)
  Support = -> [Pad006]
  sketch-geometry (4):
    g0: LineSegment StartX=115 StartY=41 StartZ=0 EndX=141 EndY=41 EndZ=0
    g1: LineSegment StartX=141 StartY=41 StartZ=0 EndX=141 EndY=61 EndZ=0
    g2: LineSegment StartX=141 StartY=61 StartZ=0 EndX=115 EndY=61 EndZ=0
    g3: LineSegment StartX=115 StartY=61 StartZ=0 EndX=115 EndY=41 EndZ=0
  constraints (8):
    c: Coincident(g0,g1)
    c: Coincident(g1,g2)
    c: Coincident(g2,g3)
    c: Coincident(g3,g0)
    c: Horizontal(g0)
    c: Horizontal(g2)
    c: Vertical(g1)
    c: Vertical(g3)
FEATURE [Sketcher::SketchObject] Sketch019
  MapMode = 5
  Placement = pos=(0,0,19.5) rot=(1,0,0;3.14159rad)
  sketch-geometry (4):
    g0: LineSegment StartX=119 StartY=57 StartZ=0 EndX=137 EndY=57 EndZ=0
    g1: LineSegment StartX=137 StartY=57 StartZ=0 EndX=137 EndY=45 EndZ=0
    g2: LineSegment StartX=137 StartY=45 StartZ=0 EndX=119 EndY=45 EndZ=0
    g3: LineSegment StartX=119 StartY=45 StartZ=0 EndX=119 EndY=57 EndZ=0
  constraints (8):
    c: Coincident(g0,g1)
    c: Coincident(g1,g2)
    c: Coincident(g2,g3)
    c: Coincident(g3,g0)
    c: Horizontal(g0)
    c: Horizontal(g2)
    c: Vertical(g1)
    c: Vertical(g3)
FEATURE [Sketcher::SketchObject] Sketch020
  MapMode = 5
  Placement = pos=(0,0,22.5) rot=(1,0,0;3.14159rad)
  sketch-geometry (1):
    g0: Circle CenterX=127 CenterY=51 CenterZ=0 NormalX=0 NormalY=0 NormalZ=1 AngleXU=0 Radius=3
FEATURE [Sketcher::SketchObject] Sketch021
  MapMode = 5
  Placement = pos=(0,21,0) rot=(0,0.707107,0.707107;3.14159rad)
  sketch-geometry (2):
    g0: Circle CenterX=-50 CenterY=12 CenterZ=0 NormalX=0 NormalY=0 NormalZ=1 AngleXU=0 Radius=3
    g1: Circle CenterX=-62 CenterY=12 CenterZ=0 NormalX=0 NormalY=0 NormalZ=1 AngleXU=0 Radius=3
FEATURE [PartDesign::Pocket] Pocket011  label="IR cutouts"
  BaseFeature = -> Pad006
  Length = 5
  Length2 = 100
  Profile = -> Sketch021
  Type = 0
FEATURE [PartDesign::Pocket] Pocket012  label="control LED cutout"
  BaseFeature = -> Pocket011
  Length = 6.5
  Length2 = 100
  Profile = -> Sketch017
  Type = 0
FEATURE [PartDesign::Pad] Pad007  label="Battery led cover"
  BaseFeature = -> Pocket012
  Length = 10.5
  Length2 = 100
  Profile = -> Sketch018
  Type = 0
FEATURE [PartDesign::Pocket] Pocket013  label="Battery LED cutout 1"
  BaseFeature = -> Pad007
  Length = 3
  Length2 = 100
  Profile = -> Sketch019
  Type = 0
FEATURE [PartDesign::Pocket] Pocket014  label="Battery LED cutout 2"
  BaseFeature = -> Pocket013
  Length = 8.5
  Length2 = 100
  Profile = -> Sketch020
  Type = 0
FEATURE [Sketcher::SketchObject] Sketch022
  MapMode = 5
  Placement = pos=(141,0,0) rot=(0.57735,-0.57735,-0.57735;2.0944rad)
  Support = -> [Pocket011]
  sketch-geometry (4):
    g0: LineSegment StartX=63 StartY=18 StartZ=0 EndX=55 EndY=18 EndZ=0
    g1: LineSegment StartX=55 StartY=18 StartZ=0 EndX=55 EndY=13 EndZ=0
    g2: LineSegment StartX=55 StartY=13 StartZ=0 EndX=63 EndY=13 EndZ=0
    g3: LineSegment StartX=63 StartY=13 StartZ=0 EndX=63 EndY=18 EndZ=0
  constraints (10):
    c: Coincident(g0,g1)
    c: Coincident(g1,g2)
    c: Coincident(g2,g3)
    c: Coincident(g3,g0)
    c: Horizontal(g0)
    c: Horizontal(g2)
    c: Vertical(g1)
    c: Vertical(g3)
    c: Distance(g1) = 5
    c: Distance(g0) = 8
FEATURE [PartDesign::Pocket] Pocket015  label="Power switch cutout"
  BaseFeature = -> Pocket014
  Length = 24
  Length2 = 100
  Profile = -> Sketch022
  Type = 0
FEATURE [Sketcher::SketchObject] Sketch023
  AttachmentOffset = pos=(100,0,0) rot=(0,0,1;0rad)
  MapMode = 5
  Placement = pos=(100,-70.7773,0) rot=(1,0,0;1.5708rad)
  Support = -> [Pocket015]
  sketch-geometry (4):
    g0: LineSegment StartX=-62 StartY=21 StartZ=0 EndX=-47 EndY=21 EndZ=0
    g1: LineSegment StartX=-47 StartY=21 StartZ=0 EndX=-47 EndY=17 EndZ=0
    g2: LineSegment StartX=-47 StartY=17 StartZ=0 EndX=-62 EndY=17 EndZ=0
    g3: LineSegment StartX=-62 StartY=17 StartZ=0 EndX=-62 EndY=21 EndZ=0
  constraints (10):
    c: Coincident(g0,g1)
    c: Coincident(g1,g2)
    c: Coincident(g2,g3)
    c: Coincident(g3,g0)
    c: Horizontal(g0)
    c: Horizontal(g2)
    c: Vertical(g1)
    c: Vertical(g3)
    c: Distance(g3) = 4
    c: Distance(g2) = 15
FEATURE [Sketcher::SketchObject] Sketch029
  MapMode = 5
  Placement = pos=(0,0,0) rot=(1,0,0;3.14159rad)
  Support = -> [Pad]
  sketch-geometry (12):
    g0: LineSegment StartX=7.99659 StartY=-16.5 StartZ=0 EndX=136 EndY=-16.5 EndZ=0
    g1: LineSegment StartX=150.5 StartY=51.0033 StartZ=0 EndX=150.5 EndY=-2 EndZ=0
    g2: LineSegment StartX=8 StartY=65.5 StartZ=0 EndX=135.999 EndY=65.5 EndZ=0
    g3: LineSegment StartX=-6.5 StartY=50.9989 StartZ=0 EndX=-6.5 EndY=-1.99856 EndZ=0
    g4: LineSegment [constr] StartX=-7 StartY=-17 StartZ=0 EndX=8.16702 EndY=-1.83304 EndZ=0
    g5: LineSegment [constr] StartX=-7 StartY=66 StartZ=0 EndX=8.16709 EndY=50.8329 EndZ=0
    g6: LineSegment [constr] StartX=151 StartY=66 StartZ=0 EndX=135.833 EndY=50.833 EndZ=0
    g7: LineSegment [constr] StartX=151 StartY=-17 StartZ=0 EndX=135.833 EndY=-1.83309 EndZ=0
    g8: ArcOfCircle CenterX=8.16709 CenterY=50.8329 CenterZ=0 NormalX=0 NormalY=0 NormalZ=1 AngleXU=0 Radius=14.668 StartAngle=1.58219 EndAngle=3.13027
    g9: ArcOfCircle CenterX=135.833 CenterY=50.833 CenterZ=0 NormalX=0 NormalY=0 NormalZ=1 AngleXU=0 Radius=14.6679 StartAngle=0.0116116 EndAngle=1.5595
    g10: ArcOfCircle CenterX=135.833 CenterY=-1.83309 CenterZ=0 NormalX=0 NormalY=0 NormalZ=1 AngleXU=0 Radius=14.6679 StartAngle=4.72377 EndAngle=6.27181
    g11: ArcOfCircle CenterX=8.16702 CenterY=-1.83304 CenterZ=0 NormalX=0 NormalY=0 NormalZ=1 AngleXU=0 Radius=14.668 StartAngle=3.15288 EndAngle=4.70077
  constraints (24):
    c: Horizontal(g0)
    c: Vertical(g1)
    c: Horizontal(g2)
    c: Vertical(g3)
    c: Coincident(g8,g5)
    c: Coincident(g9,g6)
    c: Coincident(g10,g7)
    c: Coincident(g11,g4)
    c: Coincident(g11,g3)
    c: Coincident(g11,g0)
    c: Coincident(g8,g2)
    c: Coincident(g8,g3)
    c: Coincident(g9,g1)
    c: Coincident(g9,g2)
    c: Coincident(g1,g10)
    c: Coincident(g0,g10)
    c: DistanceX(g2) = 8
    c: DistanceY(g2) = 65.5
    c: DistanceX(g3) = -6.5
    c: DistanceY(g3) = 50.9989
    c: DistanceX(g1) = 150.5
    c: DistanceY(g1) = -2
    c: DistanceX(g0) = 136
    c: DistanceY(g0) = -16.5
FEATURE [Sketcher::SketchObject] Sketch030
  MapMode = 5
  Support = -> [XY_Plane001]
  sketch-geometry (17):
    g0: GeomPoint X=9e-16 Y=15 Z=0
    g1: GeomPoint X=0 Y=-72.9216 Z=0
    g2: LineSegment StartX=4 StartY=-70.7773 StartZ=0 EndX=140 EndY=-70.7773 EndZ=0
    g3: LineSegment StartX=4 StartY=21 StartZ=0 EndX=140 EndY=21 EndZ=0
    g4: LineSegment StartX=-11 StartY=6 StartZ=0 EndX=-11 EndY=-55.7773 EndZ=0
    g5: ArcOfCircle CenterX=140 CenterY=6 CenterZ=0 NormalX=0 NormalY=0 NormalZ=1 AngleXU=0 Radius=15 StartAngle=0 EndAngle=1.5708
    g6: ArcOfCircle CenterX=140 CenterY=-55.7773 CenterZ=0 NormalX=0 NormalY=0 NormalZ=1 AngleXU=0 Radius=15 StartAngle=4.71239 EndAngle=6.28319
    g7: LineSegment StartX=155 StartY=6 StartZ=0 EndX=155 EndY=-55.7773 EndZ=0
    g8: LineSegment [constr] StartX=140 StartY=21 StartZ=0 EndX=140 EndY=6 EndZ=0
    g9: LineSegment [constr] StartX=140 StartY=6 StartZ=0 EndX=140 EndY=-70.7773 EndZ=0
    g10: LineSegment [constr] StartX=140 StartY=-55.7773 StartZ=0 EndX=155 EndY=-55.7773 EndZ=0
    g11: LineSegment [constr] StartX=155 StartY=6 StartZ=0 EndX=140 EndY=6 EndZ=0
    g12: LineSegment [constr] StartX=4 StartY=21 StartZ=0 EndX=4 EndY=-70.7773 EndZ=0
    g13: ArcOfCircle CenterX=4 CenterY=-55.7773 CenterZ=0 NormalX=0 NormalY=0 NormalZ=1 AngleXU=0 Radius=15 StartAngle=3.14159 EndAngle=4.71239
    g14: LineSegment [constr] StartX=-11 StartY=-55.7773 StartZ=0 EndX=4 EndY=-55.7773 EndZ=0
    g15: LineSegment [constr] StartX=4 StartY=6 StartZ=0 EndX=-11 EndY=6 EndZ=0
    g16: ArcOfCircle CenterX=4 CenterY=6 CenterZ=0 NormalX=0 NormalY=0 NormalZ=1 AngleXU=0 Radius=15 StartAngle=1.5708 EndAngle=3.14159
  constraints (40):
    c: PointOnObject(g1,g-2)
    c: Horizontal(g2)
    c: Horizontal(g3)
    c: Vertical(g4)
    c: Coincident(g5,g3)
    c: Coincident(g6,g2)
    c: Coincident(g7,g5)
    c: Coincident(g7,g6)
    c: Vertical(g7)
    c: Coincident(g8,g3)
    c: Coincident(g8,g5)
    c: Vertical(g8)
    c: Coincident(g9,g5)
    c: Coincident(g9,g2)
    c: Vertical(g9)
    c: PointOnObject(g6,g9)
    c: Distance(g6,g2) = 15
    c: Coincident(g10,g6)
    c: Horizontal(g10)
    c: Coincident(g6,g10)
    c: Coincident(g11,g5)
    c: Coincident(g11,g5)
    c: Vertical(g12)
    c: PointOnObject(g13,g12)
    c: Coincident(g13,g12)
    c: Coincident(g14,g4)
    c: Coincident(g14,g13)
    c: Horizontal(g14)
    c: PointOnObject(g15,g12)
    c: Horizontal(g15)
    c: Coincident(g16,g15)
    c: PointOnObject(g15,g4)
    c: Coincident(g4,g16)
    c: Coincident(g3,g12)
    c: Coincident(g13,g4)
    c: Coincident(g3,g16)
    c: Coincident(g2,g12)
    c: Distance(g13,g2) = 15
    c: Distance(g3,g16) = 15
    c: Horizontal(g11)
FEATURE [PartDesign::Pad] Pad009
  Length = 1.5
  Length2 = 100
  Profile = -> Sketch029
  Type = 0
FEATURE [PartDesign::Pocket] Pocket021
  BaseFeature = -> Pad009
  Length = 100
  Length2 = 100
  Profile = -> Sketch030
  Reversed = true
  Type = 0
FEATURE [PartDesign::Pocket] Pocket022
  BaseFeature = -> Pocket015
  Length = 5
  Length2 = 100
  Profile = -> Sketch023
  Type = 0
FEATURE [Sketcher::SketchObject] Sketch036
  MapMode = 5
  Placement = pos=(0,0,22) rot=(1,0,0;3.14159rad)
  Support = -> [Pocket022]
  sketch-geometry (13):
    g0: LineSegment StartX=69 StartY=-4 StartZ=0 EndX=70 EndY=-4 EndZ=0
    g1: LineSegment StartX=70 StartY=-4 StartZ=0 EndX=70 EndY=-2 EndZ=0
    g2: LineSegment StartX=70 StartY=-2 StartZ=0 EndX=67 EndY=-2 EndZ=0
    g3: LineSegment StartX=67 StartY=-2 StartZ=0 EndX=67 EndY=-6 EndZ=0
    g4: LineSegment StartX=67 StartY=-6 StartZ=0 EndX=68 EndY=-6 EndZ=0
    g5: LineSegment StartX=68 StartY=-6 StartZ=0 EndX=68 EndY=-4 EndZ=0
    g6: LineSegment StartX=68 StartY=-4 StartZ=0 EndX=69 EndY=-4 EndZ=0
    g7: LineSegment StartX=67 StartY=-10 StartZ=0 EndX=68 EndY=-10 EndZ=0
    g8: LineSegment StartX=68 StartY=-10 StartZ=0 EndX=68 EndY=-12 EndZ=0
    g9: LineSegment StartX=68 StartY=-12 StartZ=0 EndX=70 EndY=-12 EndZ=0
    g10: LineSegment StartX=70 StartY=-12 StartZ=0 EndX=70 EndY=-15 EndZ=0
    g11: LineSegment StartX=70 StartY=-15 StartZ=0 EndX=67 EndY=-15 EndZ=0
    g12: LineSegment StartX=67 StartY=-15 StartZ=0 EndX=67 EndY=-10 EndZ=0
  constraints (26):
    c: Horizontal(g0)
    c: Coincident(g0,g1)
    c: Vertical(g1)
    c: Coincident(g1,g2)
    c: Horizontal(g2)
    c: Coincident(g2,g3)
    c: Vertical(g3)
    c: Coincident(g3,g4)
    c: Horizontal(g4)
    c: Coincident(g4,g5)
    c: Vertical(g5)
    c: Coincident(g5,g6)
    c: Coincident(g6,g0)
    c: Horizontal(g6)
    c: Horizontal(g7)
    c: Coincident(g7,g8)
    c: Vertical(g8)
    c: Coincident(g8,g9)
    c: Horizontal(g9)
    c: Coincident(g9,g10)
    c: Vertical(g10)
    c: Coincident(g10,g11)
    c: Horizontal(g11)
    c: Coincident(g11,g12)
    c: Coincident(g12,g7)
    c: Vertical(g12)
FEATURE [PartDesign::Pad] Pad015
  BaseFeature = -> Pocket022
  Length = 6
  Length2 = 100
  Profile = -> Sketch036
  Type = 0
FEATURE [PartDesign::Fillet] Fillet
  Base = -> Pad015 [Edge335]
  BaseFeature = -> Pad015
  Radius = 7
FEATURE [PartDesign::Chamfer] Chamfer
  Base = -> Fillet [Edge14]
  BaseFeature = -> Fillet
  Size = 3.5
FEATURE [Sketcher::SketchObject] Sketch037
  MapMode = 5
  Placement = pos=(0,17,0) rot=(1,0,0;1.5708rad)
  Support = -> [Chamfer]
  sketch-geometry (2):
    g0: Circle CenterX=62 CenterY=12 CenterZ=0 NormalX=0 NormalY=0 NormalZ=1 AngleXU=0 Radius=3
    g1: Circle CenterX=62 CenterY=12 CenterZ=0 NormalX=0 NormalY=0 NormalZ=1 AngleXU=0 Radius=5
  constraints (1):
    c: Coincident(g1,g0)
FEATURE [PartDesign::Pad] Pad016
  BaseFeature = -> Chamfer
  Length = 3
  Length2 = 100
  Profile = -> Sketch037
  Type = 0
FEATURE [Sketcher::SketchObject] Sketch038
  MapMode = 5
  Placement = pos=(155,0,0) rot=(0.57735,0.57735,0.57735;2.0944rad)
  Support = -> [Pad016]
  sketch-geometry (5):
    g0: LineSegment [constr] StartX=-53 StartY=17 StartZ=0 EndX=-39 EndY=17 EndZ=0
    g1: LineSegment StartX=-53 StartY=22 StartZ=0 EndX=-39 EndY=22 EndZ=0
    g2: LineSegment StartX=-39 StartY=22 StartZ=0 EndX=-39 EndY=12 EndZ=0
    g3: LineSegment StartX=-39 StartY=12 StartZ=0 EndX=-53 EndY=12 EndZ=0
    g4: LineSegment StartX=-53 StartY=12 StartZ=0 EndX=-53 EndY=22 EndZ=0
  constraints (9):
    c: Horizontal(g0)
    c: Coincident(g1,g2)
    c: Coincident(g2,g3)
    c: Coincident(g3,g4)
    c: Coincident(g4,g1)
    c: Horizontal(g1)
    c: Horizontal(g3)
    c: Vertical(g2)
    c: Vertical(g4)
FEATURE [PartDesign::Pocket] Pocket023
  BaseFeature = -> Pad016
  Length = 5
  Length2 = 100
  Profile = -> Sketch038
  Type = 0
FEATURE [Sketcher::SketchObject] Sketch039
  MapMode = 5
  Placement = pos=(151,0,0) rot=(0.57735,-0.57735,-0.57735;2.0944rad)
  Support = -> [Pocket023]
  sketch-geometry (8):
    g0: LineSegment StartX=53 StartY=12 StartZ=0 EndX=39 EndY=12 EndZ=0
    g1: LineSegment StartX=39 StartY=12 StartZ=0 EndX=39 EndY=22 EndZ=0
    g2: LineSegment StartX=39 StartY=22 StartZ=0 EndX=53 EndY=22 EndZ=0
    g3: LineSegment StartX=53 StartY=22 StartZ=0 EndX=53 EndY=12 EndZ=0
    g4: LineSegment StartX=54 StartY=11 StartZ=0 EndX=38 EndY=11 EndZ=0
    g5: LineSegment StartX=38 StartY=11 StartZ=0 EndX=38 EndY=23 EndZ=0
    g6: LineSegment StartX=38 StartY=23 StartZ=0 EndX=54 EndY=23 EndZ=0
    g7: LineSegment StartX=54 StartY=23 StartZ=0 EndX=54 EndY=11 EndZ=0
  constraints (16):
    c: Coincident(g0,g1)
    c: Coincident(g1,g2)
    c: Coincident(g2,g3)
    c: Coincident(g3,g0)
    c: Horizontal(g0)
    c: Horizontal(g2)
    c: Vertical(g1)
    c: Vertical(g3)
    c: Coincident(g4,g5)
    c: Coincident(g5,g6)
    c: Coincident(g6,g7)
    c: Coincident(g7,g4)
    c: Horizontal(g4)
    c: Horizontal(g6)
    c: Vertical(g5)
    c: Vertical(g7)
FEATURE [PartDesign::Pad] Pad017
  BaseFeature = -> Pocket023
  Length = 6
  Length2 = 100
  Profile = -> Sketch039
  Type = 0
FEATURE [Sketcher::SketchObject] Sketch040
  MapMode = 5
  Placement = pos=(145,0,0) rot=(0.57735,-0.57735,-0.57735;2.0944rad)
  Support = -> [Pad017]
  sketch-geometry (8):
    g0: LineSegment StartX=38 StartY=19.5 StartZ=0 EndX=39 EndY=19.5 EndZ=0
    g1: LineSegment StartX=39 StartY=19.5 StartZ=0 EndX=39 EndY=22 EndZ=0
    g2: LineSegment StartX=39 StartY=22 StartZ=0 EndX=53 EndY=22 EndZ=0
    g3: LineSegment StartX=53 StartY=22 StartZ=0 EndX=53 EndY=19.5 EndZ=0
    g4: LineSegment StartX=53 StartY=19.5 StartZ=0 EndX=54 EndY=19.5 EndZ=0
    g5: LineSegment StartX=54 StartY=19.5 StartZ=0 EndX=54 EndY=23 EndZ=0
    g6: LineSegment StartX=54 StartY=23 StartZ=0 EndX=38 EndY=23 EndZ=0
    g7: LineSegment StartX=38 StartY=23 StartZ=0 EndX=38 EndY=19.5 EndZ=0
  constraints (16):
    c: Horizontal(g0)
    c: Coincident(g0,g1)
    c: Vertical(g1)
    c: Coincident(g1,g2)
    c: Horizontal(g2)
    c: Coincident(g2,g3)
    c: Vertical(g3)
    c: Coincident(g3,g4)
    c: Horizontal(g4)
    c: Coincident(g4,g5)
    c: Vertical(g5)
    c: Coincident(g5,g6)
    c: Horizontal(g6)
    c: Coincident(g6,g7)
    c: Vertical(g7)
    c: Coincident(g0,g7)
FEATURE [PartDesign::Pad] Pad018
  BaseFeature = -> Pad017
  Length = 7
  Length2 = 100
  Profile = -> Sketch040
  Type = 0
FEATURE [Sketcher::SketchObject] Sketch041
  MapMode = 5
  Placement = pos=(0,0,22) rot=(1,0,0;3.14159rad)
  Support = -> [Pad018]
  sketch-geometry (4):
    g0: LineSegment StartX=138 StartY=41 StartZ=0 EndX=141 EndY=41 EndZ=0
    g1: LineSegment StartX=141 StartY=41 StartZ=0 EndX=141 EndY=39 EndZ=0
    g2: LineSegment StartX=141 StartY=39 StartZ=0 EndX=138 EndY=39 EndZ=0
    g3: LineSegment StartX=138 StartY=39 StartZ=0 EndX=138 EndY=41 EndZ=0
  constraints (8):
    c: Coincident(g0,g1)
    c: Coincident(g1,g2)
    c: Coincident(g2,g3)
    c: Coincident(g3,g0)
    c: Horizontal(g0)
    c: Horizontal(g2)
    c: Vertical(g1)
    c: Vertical(g3)
FEATURE [PartDesign::Pad] Pad019
  BaseFeature = -> Pad018
  Length = 2.5
  Length2 = 100
  Profile = -> Sketch041
  Type = 0
FEATURE [Sketcher::SketchObject] Sketch042
  MapMode = 5
  Placement = pos=(0,0,22) rot=(1,0,0;3.14159rad)
  Support = -> [Pad019]
  sketch-geometry (4):
    g0: LineSegment StartX=138 StartY=54 StartZ=0 EndX=151 EndY=54 EndZ=0
    g1: LineSegment StartX=151 StartY=54 StartZ=0 EndX=151 EndY=38 EndZ=0
    g2: LineSegment StartX=151 StartY=38 StartZ=0 EndX=138 EndY=38 EndZ=0
    g3: LineSegment StartX=138 StartY=38 StartZ=0 EndX=138 EndY=54 EndZ=0
  constraints (8):
    c: Coincident(g0,g1)
    c: Coincident(g1,g2)
    c: Coincident(g2,g3)
    c: Coincident(g3,g0)
    c: Horizontal(g0)
    c: Horizontal(g2)
    c: Vertical(g1)
    c: Vertical(g3)
FEATURE [PartDesign::Pad] Pad020
  BaseFeature = -> Pad019
  Length = 8
  Length2 = 100
  Profile = -> Sketch042
  Reversed = true
  Type = 0
FEATURE [Sketcher::SketchObject] Sketch043
  MapMode = 5
  Placement = pos=(0,0,30) rot=(1,0,0;3.14159rad)
  Support = -> [Pad020]
  sketch-geometry (4):
    g0: LineSegment StartX=143 StartY=2 StartZ=0 EndX=107 EndY=2 EndZ=0
    g1: LineSegment StartX=107 StartY=2 StartZ=0 EndX=107 EndY=-4 EndZ=0
    g2: LineSegment StartX=107 StartY=-4 StartZ=0 EndX=143 EndY=-4 EndZ=0
    g3: LineSegment StartX=143 StartY=-4 StartZ=0 EndX=143 EndY=2 EndZ=0
  constraints (8):
    c: Coincident(g0,g1)
    c: Coincident(g1,g2)
    c: Coincident(g2,g3)
    c: Coincident(g3,g0)
    c: Horizontal(g0)
    c: Horizontal(g2)
    c: Vertical(g1)
    c: Vertical(g3)
FEATURE [PartDesign::Pad] Pad021
  BaseFeature = -> Pad020
  Length = 5.5
  Length2 = 100
  Profile = -> Sketch043
  Type = 0
FEATURE [Sketcher::SketchObject] Sketch044
  MapMode = 5
  Placement = pos=(0,0,30) rot=(1,0,0;3.14159rad)
  Support = -> [Pad021]
  sketch-geometry (18):
    g0: LineSegment StartX=26 StartY=49 StartZ=0 EndX=91 EndY=49 EndZ=0
    g1: LineSegment StartX=91 StartY=49 StartZ=0 EndX=91 EndY=48 EndZ=0
    g2: LineSegment StartX=91 StartY=48 StartZ=0 EndX=26 EndY=48 EndZ=0
    g3: LineSegment StartX=26 StartY=48 StartZ=0 EndX=26 EndY=49 EndZ=0
    g4: LineSegment StartX=104 StartY=49 StartZ=0 EndX=105 EndY=49 EndZ=0
    g5: LineSegment StartX=105 StartY=49 StartZ=0 EndX=105 EndY=30 EndZ=0
    g6: LineSegment StartX=104 StartY=2 StartZ=0 EndX=104 EndY=26 EndZ=0
    g7: LineSegment StartX=105 StartY=2 StartZ=0 EndX=107 EndY=2 EndZ=0
    g8: LineSegment StartX=107 StartY=2 StartZ=0 EndX=107 EndY=-2 EndZ=0
    g9: LineSegment StartX=104 StartY=-2 StartZ=0 EndX=104 EndY=2 EndZ=0
    g10: LineSegment StartX=70 StartY=-2 StartZ=0 EndX=104 EndY=-2 EndZ=0
    g11: LineSegment StartX=107 StartY=-2 StartZ=0 EndX=107 EndY=-4 EndZ=0
    g12: LineSegment StartX=107 StartY=-4 StartZ=0 EndX=70 EndY=-4 EndZ=0
    g13: LineSegment StartX=70 StartY=-4 StartZ=0 EndX=70 EndY=-2 EndZ=0
    g14: LineSegment StartX=105 StartY=30 StartZ=0 EndX=104 EndY=30 EndZ=0
    g15: LineSegment StartX=104 StartY=26 StartZ=0 EndX=105 EndY=26 EndZ=0
    g16: LineSegment StartX=105 StartY=26 StartZ=0 EndX=105 EndY=2 EndZ=0
    g17: LineSegment StartX=104 StartY=30 StartZ=0 EndX=104 EndY=49 EndZ=0
  constraints (35):
    c: Coincident(g0,g1)
    c: Coincident(g1,g2)
    c: Coincident(g2,g3)
    c: Coincident(g3,g0)
    c: Horizontal(g0)
    c: Horizontal(g2)
    c: Vertical(g1)
    c: Vertical(g3)
    c: Coincident(g4,g5)
    c: Coincident(g17,g4)
    c: Horizontal(g4)
    c: Vertical(g5)
    c: Vertical(g6)
    c: Coincident(g16,g7)
    c: Horizontal(g7)
    c: Coincident(g7,g8)
    c: Vertical(g8)
    c: Coincident(g9,g6)
    c: Vertical(g9)
    c: Coincident(g11,g12)
    c: Coincident(g12,g13)
    c: Coincident(g13,g10)
    c: Horizontal(g10)
    c: Horizontal(g12)
    c: Vertical(g11)
    c: Vertical(g13)
    c: Coincident(g8,g11)
    c: Horizontal(g14)
    c: Horizontal(g15)
    c: Tangent(g5,g16)
    c: Tangent(g6,g17)
    c: Coincident(g14,g5)
    c: Coincident(g14,g17)
    c: Coincident(g15,g6)
    c: Coincident(g15,g16)
FEATURE [PartDesign::Pad] Pad022
  BaseFeature = -> Pad021
  Length = 4
  Length2 = 100
  Profile = -> Sketch044
  Type = 0
FEATURE [Sketcher::SketchObject] Sketch045
  MapMode = 5
  Placement = pos=(0,0,11) rot=(1,0,0;3.14159rad)
  Support = -> [Pad022]
  sketch-geometry (4):
    g0: LineSegment StartX=145 StartY=38 StartZ=0 EndX=147 EndY=38 EndZ=0
    g1: LineSegment StartX=147 StartY=38 StartZ=0 EndX=147 EndY=54 EndZ=0
    g2: LineSegment StartX=147 StartY=54 StartZ=0 EndX=145 EndY=54 EndZ=0
    g3: LineSegment StartX=145 StartY=54 StartZ=0 EndX=145 EndY=38 EndZ=0
  constraints (8):
    c: Coincident(g0,g1)
    c: Coincident(g1,g2)
    c: Coincident(g2,g3)
    c: Coincident(g3,g0)
    c: Horizontal(g0)
    c: Horizontal(g2)
    c: Vertical(g1)
    c: Vertical(g3)
FEATURE [PartDesign::Pocket] Pocket024
  BaseFeature = -> Pad022
  Length = 2
  Length2 = 100
  Profile = -> Sketch045
  Type = 0
FEATURE [Sketcher::SketchObject] Sketch046
  MapMode = 5
  Placement = pos=(0,0,30) rot=(1,0,0;3.14159rad)
  sketch-geometry (1):
    g0: Circle CenterX=101 CenterY=55 CenterZ=0 NormalX=0 NormalY=0 NormalZ=1 AngleXU=0 Radius=2.5
FEATURE [PartDesign::Pad] Pad023
  Length = 2.5
  Length2 = 100
  Placement = pos=(0,0,30) rot=(1,0,0;3.14159rad)
  Profile = -> Sketch046
  Reversed = true
  Type = 0
FEATURE [Sketcher::SketchObject] Sketch047
  MapMode = 5
  Placement = pos=(0,0,32.5) rot=(0,0,1;0rad)
  Support = -> [Pad023]
  sketch-geometry (1):
    g0: Circle CenterX=101 CenterY=-55 CenterZ=0 NormalX=0 NormalY=0 NormalZ=1 AngleXU=0 Radius=5
FEATURE [PartDesign::Pad] Pad024
  BaseFeature = -> Pad023
  Length = 3
  Length2 = 100
  Placement = pos=(0,0,30) rot=(1,0,0;3.14159rad)
  Profile = -> Sketch047
  Type = 0
FEATURE [PartDesign::Fillet] Fillet003
  Base = -> Pad024 [Edge3]
  BaseFeature = -> Pad024
  Placement = pos=(0,0,30) rot=(1,0,0;3.14159rad)
  Radius = 1.5
FEATURE [Sketcher::SketchObject] Sketch049
  MapMode = 5
  Placement = pos=(0,0,30) rot=(1,0,0;3.14159rad)
  sketch-geometry (1):
    g0: Circle CenterX=101 CenterY=55 CenterZ=0 NormalX=0 NormalY=0 NormalZ=1 AngleXU=0 Radius=2.5
FEATURE [PartDesign::Pad] Pad025
  BaseFeature = -> Fillet003
  Length = 4
  Length2 = 100
  Placement = pos=(0,0,30) rot=(1,0,0;3.14159rad)
  Profile = -> Sketch049
  Type = 0
FEATURE [PartDesign::ShapeBinder] CopyPocket026
  Placement = pos=(0,0,30) rot=(1,0,0;3.14159rad)
  TraceSupport = false
FEATURE [Sketcher::SketchObject] Sketch051
  MapMode = 5
  Placement = pos=(-1.9e-15,3.3e-15,26) rot=(1,0,0;3.14159rad)
  Support = -> [CopyPocket026]
  sketch-geometry (14):
    g0: LineSegment StartX=95 StartY=61.5 StartZ=0 EndX=94.5 EndY=61.5 EndZ=0
    g1: LineSegment StartX=94.5 StartY=61.5 StartZ=0 EndX=94.5 EndY=61 EndZ=0
    g2: LineSegment StartX=94.5 StartY=61 StartZ=0 EndX=98.5 EndY=57 EndZ=0
    g3: LineSegment StartX=95 StartY=61.5 StartZ=0 EndX=99 EndY=57.5 EndZ=0
    g4: LineSegment StartX=107.5 StartY=48.5 StartZ=0 EndX=107.5 EndY=49 EndZ=0
    g5: LineSegment StartX=107.5 StartY=49 StartZ=0 EndX=103.5 EndY=53 EndZ=0
    g6: LineSegment StartX=107.5 StartY=48.5 StartZ=0 EndX=107 EndY=48.5 EndZ=0
    g7: LineSegment StartX=107 StartY=48.5 StartZ=0 EndX=103 EndY=52.5 EndZ=0
    g8: LineSegment StartX=98.5 StartY=55 StartZ=0 EndX=98.5 EndY=57 EndZ=0
    g9: LineSegment StartX=99 StartY=57.5 StartZ=0 EndX=101 EndY=57.5 EndZ=0
    g10: LineSegment StartX=103.5 StartY=53 StartZ=0 EndX=103.5 EndY=55 EndZ=0
    g11: LineSegment StartX=103 StartY=52.5 StartZ=0 EndX=101 EndY=52.5 EndZ=0
    g12: ArcOfCircle CenterX=101 CenterY=55 CenterZ=0 NormalX=0 NormalY=0 NormalZ=1 AngleXU=0 Radius=2.5 StartAngle=0 EndAngle=1.5708
    g13: ArcOfCircle CenterX=101 CenterY=55 CenterZ=0 NormalX=0 NormalY=0 NormalZ=1 AngleXU=0 Radius=2.5 StartAngle=3.14159 EndAngle=4.71239
  constraints (21):
    c: Horizontal(g0)
    c: Coincident(g0,g1)
    c: Vertical(g1)
    c: Coincident(g1,g2)
    c: Coincident(g0,g3)
    c: Vertical(g4)
    c: Coincident(g4,g5)
    c: Coincident(g4,g6)
    c: Horizontal(g6)
    c: Coincident(g6,g7)
    c: Coincident(g9,g3)
    c: Horizontal(g9)
    c: Coincident(g10,g5)
    c: Vertical(g10)
    c: Coincident(g11,g7)
    c: Horizontal(g11)
    c: Coincident(g12,g9)
    c: Coincident(g12,g10)
    c: Coincident(g13,g12)
    c: Coincident(g13,g8)
    c: Coincident(g13,g11)
FEATURE [PartDesign::Pad] Pad026
  Length = 4
  Length2 = 100
  Placement = pos=(0,0,30) rot=(1,0,0;3.14159rad)
  Profile = -> Sketch051
  Type = 0
FEATURE [Sketcher::SketchObject] Sketch052
  MapMode = 5
  Placement = pos=(-2.5e-15,4.8e-15,26) rot=(0,0,1;0rad)
  Support = -> [Pad026]
  sketch-geometry (1):
    g0: Circle CenterX=101 CenterY=-55 CenterZ=0 NormalX=0 NormalY=0 NormalZ=1 AngleXU=0 Radius=1.17267
FEATURE [PartDesign::Pad] Pad027
  BaseFeature = -> Pad026
  Length = 3.5
  Length2 = 100
  Placement = pos=(0,0,30) rot=(1,0,0;3.14159rad)
  Profile = -> Sketch052
  Type = 0
FEATURE [Sketcher::SketchObject] Sketch053
  MapMode = 5
  Placement = pos=(-5e-15,9.5e-15,22) rot=(1,0,0;3.14159rad)
  Support = -> [Pad027]
  sketch-geometry (1):
    g0: Circle CenterX=101 CenterY=55 CenterZ=0 NormalX=0 NormalY=0 NormalZ=1 AngleXU=0 Radius=5
FEATURE [PartDesign::Pad] Pad028
  BaseFeature = -> Pad027
  Length = 3.25
  Length2 = 100
  Placement = pos=(0,0,30) rot=(1,0,0;3.14159rad)
  Profile = -> Sketch053
  Type = 0
FEATURE [Sketcher::SketchObject] Sketch054
  AttachmentOffset = pos=(0,0,-2) rot=(0,0,1;0rad)
  MapMode = 5
  Placement = pos=(0,0,2) rot=(1,0,0;3.14159rad)
  Support = -> [Pocket024]
  sketch-geometry (16):
    g0: LineSegment StartX=-8 StartY=-5 StartZ=0 EndX=5 EndY=-5 EndZ=0
    g1: LineSegment StartX=5 StartY=-5 StartZ=0 EndX=5 EndY=-18 EndZ=0
    g2: LineSegment StartX=5 StartY=-18 StartZ=0 EndX=-4 EndY=-16 EndZ=0
    g3: LineSegment StartX=-4 StartY=-16 StartZ=0 EndX=-8 EndY=-5 EndZ=0
    g4: LineSegment StartX=-1 StartY=59 StartZ=0 EndX=-1 EndY=51.7865 EndZ=0
    g5: LineSegment StartX=-1 StartY=51.7865 StartZ=0 EndX=-8 EndY=51.7865 EndZ=0
    g6: LineSegment StartX=-8 StartY=51.7865 StartZ=0 EndX=-8 EndY=59 EndZ=0
    g7: LineSegment StartX=-8 StartY=59 StartZ=0 EndX=-1 EndY=59 EndZ=0
    g8: LineSegment StartX=151.454 StartY=-1 StartZ=0 EndX=145 EndY=-1 EndZ=0
    g9: LineSegment StartX=145 StartY=-1 StartZ=0 EndX=145 EndY=-15 EndZ=0
    g10: LineSegment StartX=145 StartY=-15 StartZ=0 EndX=151.454 EndY=-15 EndZ=0
    g11: LineSegment StartX=151.454 StartY=-15 StartZ=0 EndX=151.454 EndY=-1 EndZ=0
    g12: LineSegment StartX=147 StartY=63 StartZ=0 EndX=151 EndY=63 EndZ=0
    g13: LineSegment StartX=151 StartY=63 StartZ=0 EndX=151 EndY=54 EndZ=0
    g14: LineSegment StartX=151 StartY=54 StartZ=0 EndX=147 EndY=54 EndZ=0
    g15: LineSegment StartX=147 StartY=54 StartZ=0 EndX=147 EndY=63 EndZ=0
  constraints (30):
    c: Horizontal(g0)
    c: Coincident(g0,g1)
    c: Vertical(g1)
    c: Coincident(g1,g2)
    c: Coincident(g2,g3)
    c: Coincident(g3,g0)
    c: Vertical(g4)
    c: Coincident(g4,g5)
    c: Horizontal(g5)
    c: Coincident(g5,g6)
    c: Vertical(g6)
    c: Coincident(g6,g7)
    c: Coincident(g7,g4)
    c: Horizontal(g7)
    c: Coincident(g8,g9)
    c: Coincident(g9,g10)
    c: Coincident(g10,g11)
    c: Coincident(g11,g8)
    c: Horizontal(g8)
    c: Horizontal(g10)
    c: Vertical(g9)
    c: Vertical(g11)
    c: Coincident(g12,g13)
    c: Coincident(g13,g14)
    c: Coincident(g14,g15)
    c: Coincident(g15,g12)
    c: Horizontal(g12)
    c: Horizontal(g14)
    c: Vertical(g13)
    c: Vertical(g15)
FEATURE [PartDesign::Pad] Pad029
  BaseFeature = -> Pocket024
  Length = 6
  Length2 = 100
  Profile = -> Sketch054
  Reversed = true
  Type = 0
FEATURE [Sketcher::SketchObject] Sketch055
  MapMode = 5
  Placement = pos=(-1.9e-15,3.3e-15,26) rot=(1,0,0;3.14159rad)
  Support = -> [CopyPocket026]
  sketch-geometry (14):
    g0: LineSegment StartX=95 StartY=61.5 StartZ=0 EndX=94.5 EndY=61.5 EndZ=0
    g1: LineSegment StartX=94.5 StartY=61.5 StartZ=0 EndX=94.5 EndY=61 EndZ=0
    g2: LineSegment StartX=94.5 StartY=61 StartZ=0 EndX=98.5 EndY=57 EndZ=0
    g3: LineSegment StartX=95 StartY=61.5 StartZ=0 EndX=99 EndY=57.5 EndZ=0
    g4: LineSegment StartX=107.5 StartY=48.5 StartZ=0 EndX=107.5 EndY=49 EndZ=0
    g5: LineSegment StartX=107.5 StartY=49 StartZ=0 EndX=103.5 EndY=53 EndZ=0
    g6: LineSegment StartX=107.5 StartY=48.5 StartZ=0 EndX=107 EndY=48.5 EndZ=0
    g7: LineSegment StartX=107 StartY=48.5 StartZ=0 EndX=103 EndY=52.5 EndZ=0
    g8: LineSegment StartX=98.5 StartY=56 StartZ=0 EndX=98.5 EndY=57 EndZ=0
    g9: LineSegment StartX=99 StartY=57.5 StartZ=0 EndX=100 EndY=57.5 EndZ=0
    g10: LineSegment StartX=103.5 StartY=53 StartZ=0 EndX=103.5 EndY=54 EndZ=0
    g11: LineSegment StartX=103 StartY=52.5 StartZ=0 EndX=102 EndY=52.5 EndZ=0
    g12: ArcOfCircle CenterX=101 CenterY=55 CenterZ=0 NormalX=0 NormalY=0 NormalZ=1 AngleXU=0 Radius=2.69258 StartAngle=1.9513 EndAngle=2.76109
    g13: ArcOfCircle CenterX=101 CenterY=55 CenterZ=0 NormalX=0 NormalY=0 NormalZ=1 AngleXU=0 Radius=2.69258 StartAngle=5.0929 EndAngle=5.90268
  constraints (21):
    c: Horizontal(g0)
    c: Coincident(g0,g1)
    c: Vertical(g1)
    c: Coincident(g1,g2)
    c: Coincident(g0,g3)
    c: Vertical(g4)
    c: Coincident(g4,g5)
    c: Coincident(g4,g6)
    c: Horizontal(g6)
    c: Coincident(g6,g7)
    c: Coincident(g9,g3)
    c: Horizontal(g9)
    c: Coincident(g10,g5)
    c: Vertical(g10)
    c: Coincident(g11,g7)
    c: Horizontal(g11)
    c: Coincident(g12,g8)
    c: Coincident(g12,g9)
    c: Coincident(g13,g12)
    c: Coincident(g13,g10)
    c: Coincident(g13,g11)
FEATURE [PartDesign::Pad] Pad030
  BaseFeature = -> Pad028
  Length = 2
  Length2 = 100
  Placement = pos=(0,0,30) rot=(1,0,0;3.14159rad)
  Profile = -> Sketch055
  Reversed = true
  Type = 0
FEATURE [PartDesign::Body] Body003  label="tlacitko_dolni"
  Group = -> [CopyPocket026,Sketch051,Pad026,Sketch052,Pad027,Sketch053,Pad028,Sketch055,Pad030]
  Origin = -> Origin003
  Placement = pos=(75,0,0) rot=(0,0,1;0rad)
  Tip = -> Pad030
FEATURE [Sketcher::SketchObject] Sketch056
  MapMode = 5
  Placement = pos=(157,0,0) rot=(0.57735,0.57735,0.57735;2.0944rad)
  sketch-geometry (4):
    g0: LineSegment StartX=-62.5 StartY=17.5 StartZ=0 EndX=-58.5 EndY=17.5 EndZ=0
    g1: LineSegment StartX=-58.5 StartY=17.5 StartZ=0 EndX=-58.5 EndY=13.5 EndZ=0
    g2: LineSegment StartX=-58.5 StartY=13.5 StartZ=0 EndX=-62.5 EndY=13.5 EndZ=0
    g3: LineSegment StartX=-62.5 StartY=13.5 StartZ=0 EndX=-62.5 EndY=17.5 EndZ=0
  constraints (8):
    c: Coincident(g0,g1)
    c: Coincident(g1,g2)
    c: Coincident(g2,g3)
    c: Coincident(g3,g0)
    c: Horizontal(g0)
    c: Horizontal(g2)
    c: Vertical(g1)
    c: Vertical(g3)
FEATURE [PartDesign::Pad] Pad031
  Length = 15
  Length2 = 100
  Placement = pos=(157,0,0) rot=(0.57735,0.57735,0.57735;2.0944rad)
  Profile = -> Sketch056
  Reversed = true
  Type = 0
FEATURE [Sketcher::SketchObject] Sketch057
  MapMode = 5
  Placement = pos=(142,0,0) rot=(0.57735,0.57735,-0.57735;4.18879rad)
  Support = -> [Pad031]
  sketch-geometry (4):
    g0: LineSegment StartX=-61.75 StartY=-13.5 StartZ=0 EndX=-59.25 EndY=-13.5 EndZ=0
    g1: LineSegment StartX=-59.25 StartY=-13.5 StartZ=0 EndX=-59.25 EndY=-16.75 EndZ=0
    g2: LineSegment StartX=-59.25 StartY=-16.75 StartZ=0 EndX=-61.75 EndY=-16.75 EndZ=0
    g3: LineSegment StartX=-61.75 StartY=-16.75 StartZ=0 EndX=-61.75 EndY=-13.5 EndZ=0
  constraints (8):
    c: Coincident(g0,g1)
    c: Coincident(g1,g2)
    c: Coincident(g2,g3)
    c: Coincident(g3,g0)
    c: Horizontal(g0)
    c: Horizontal(g2)
    c: Vertical(g1)
    c: Vertical(g3)
FEATURE [PartDesign::Pocket] Pocket027
  BaseFeature = -> Pad031
  Length = 4.5
  Length2 = 100
  Placement = pos=(157,0,0) rot=(0.57735,0.57735,0.57735;2.0944rad)
  Profile = -> Sketch057
  Type = 0
FEATURE [Sketcher::SketchObject] Sketch058
  MapMode = 5
  Placement = pos=(0,0,11) rot=(1,0,0;3.14159rad)
  Support = -> [Pad029]
  sketch-geometry (4):
    g0: LineSegment StartX=151 StartY=54 StartZ=0 EndX=147 EndY=54 EndZ=0
    g1: LineSegment StartX=147 StartY=54 StartZ=0 EndX=147 EndY=63 EndZ=0
    g2: LineSegment StartX=147 StartY=63 StartZ=0 EndX=151 EndY=63 EndZ=0
    g3: LineSegment StartX=151 StartY=63 StartZ=0 EndX=151 EndY=54 EndZ=0
  constraints (8):
    c: Coincident(g0,g1)
    c: Coincident(g1,g2)
    c: Coincident(g2,g3)
    c: Coincident(g3,g0)
    c: Horizontal(g0)
    c: Horizontal(g2)
    c: Vertical(g1)
    c: Vertical(g3)
FEATURE [PartDesign::Pad] Pad032
  BaseFeature = -> Pad029
  Length = 18
  Length2 = 100
  Profile = -> Sketch058
  Reversed = true
  Type = 2
FEATURE [Sketcher::SketchObject] Sketch059
  MapMode = 5
  Placement = pos=(0,0,11) rot=(1,0,0;3.14159rad)
  Support = -> [Pad032]
  sketch-geometry (4):
    g0: LineSegment StartX=147 StartY=49 StartZ=0 EndX=151 EndY=49 EndZ=0
    g1: LineSegment StartX=151 StartY=49 StartZ=0 EndX=151 EndY=61.7795 EndZ=0
    g2: LineSegment StartX=151 StartY=61.7795 StartZ=0 EndX=147 EndY=61.7795 EndZ=0
    g3: LineSegment StartX=147 StartY=61.7795 StartZ=0 EndX=147 EndY=49 EndZ=0
  constraints (8):
    c: Coincident(g0,g1)
    c: Coincident(g1,g2)
    c: Coincident(g2,g3)
    c: Coincident(g3,g0)
    c: Horizontal(g0)
    c: Horizontal(g2)
    c: Vertical(g1)
    c: Vertical(g3)
FEATURE [PartDesign::Pad] Pad033
  BaseFeature = -> Pad032
  Length = 10
  Length2 = 100
  Profile = -> Sketch059
  Type = 2
FEATURE [Sketcher::SketchObject] Sketch060
  AttachmentOffset = pos=(0,0,-7) rot=(0,0,1;0rad)
  MapMode = 5
  Placement = pos=(0,0,18) rot=(1,0,0;3.14159rad)
  Support = -> [Pad032]
  sketch-geometry (4):
    g0: LineSegment StartX=145 StartY=54 StartZ=0 EndX=151 EndY=54 EndZ=0
    g1: LineSegment StartX=151 StartY=54 StartZ=0 EndX=151 EndY=63 EndZ=0
    g2: LineSegment StartX=151 StartY=63 StartZ=0 EndX=145 EndY=63 EndZ=0
    g3: LineSegment StartX=145 StartY=63 StartZ=0 EndX=145 EndY=54 EndZ=0
  constraints (8):
    c: Coincident(g0,g1)
    c: Coincident(g1,g2)
    c: Coincident(g2,g3)
    c: Coincident(g3,g0)
    c: Horizontal(g0)
    c: Horizontal(g2)
    c: Vertical(g1)
    c: Vertical(g3)
FEATURE [PartDesign::Pad] Pad034
  BaseFeature = -> Pad033
  Length = 10
  Length2 = 100
  Profile = -> Sketch060
  Reversed = true
  Type = 2
FEATURE [PartDesign::Chamfer] Chamfer001
  Base = -> Pad034 [Edge814]
  BaseFeature = -> Pad034
  Size = 4.99
FEATURE [Sketcher::SketchObject] Sketch061
  MapMode = 5
  Placement = pos=(147,0,0) rot=(0.57735,-0.57735,-0.57735;2.0944rad)
  Support = -> [Chamfer001]
  sketch-geometry (8):
    g0: LineSegment StartX=62 StartY=13 StartZ=0 EndX=62 EndY=11 EndZ=0
    g1: LineSegment StartX=62 StartY=11 StartZ=0 EndX=67 EndY=11 EndZ=0
    g2: LineSegment StartX=67 StartY=11 StartZ=0 EndX=67 EndY=8 EndZ=0
    g3: LineSegment StartX=67 StartY=8 StartZ=0 EndX=51 EndY=8 EndZ=0
    g4: LineSegment StartX=51 StartY=8 StartZ=0 EndX=51 EndY=11 EndZ=0
    g5: LineSegment StartX=51 StartY=11 StartZ=0 EndX=56 EndY=11 EndZ=0
    g6: LineSegment StartX=56 StartY=11 StartZ=0 EndX=56 EndY=13 EndZ=0
    g7: LineSegment StartX=56 StartY=13 StartZ=0 EndX=62 EndY=13 EndZ=0
  constraints (16):
    c: Vertical(g0)
    c: Coincident(g0,g1)
    c: Horizontal(g1)
    c: Coincident(g1,g2)
    c: Vertical(g2)
    c: Coincident(g2,g3)
    c: Horizontal(g3)
    c: Coincident(g3,g4)
    c: Vertical(g4)
    c: Coincident(g4,g5)
    c: Horizontal(g5)
    c: Coincident(g5,g6)
    c: Vertical(g6)
    c: Coincident(g6,g7)
    c: Coincident(g7,g0)
    c: Horizontal(g7)
FEATURE [PartDesign::Pocket] Pocket028
  BaseFeature = -> Chamfer001
  Length = 1
  Length2 = 100
  Profile = -> Sketch061
  Type = 0
FEATURE [Sketcher::SketchObject] Sketch062
  AttachmentOffset = pos=(0,0,0.5) rot=(0,0,1;0rad)
  MapMode = 5
  Placement = pos=(146.5,0,0) rot=(0.57735,-0.57735,-0.57735;2.0944rad)
  Support = -> [Chamfer001]
  sketch-geometry (8):
    g0: LineSegment StartX=61.75 StartY=13.5 StartZ=0 EndX=61.75 EndY=10.75 EndZ=0
    g1: LineSegment StartX=61.75 StartY=10.75 StartZ=0 EndX=66.75 EndY=10.75 EndZ=0
    g2: LineSegment StartX=66.75 StartY=10.75 StartZ=0 EndX=66.75 EndY=8.25 EndZ=0
    g3: LineSegment StartX=66.75 StartY=8.25 StartZ=0 EndX=54.25 EndY=8.25 EndZ=0
    g4: LineSegment StartX=54.25 StartY=8.25 StartZ=0 EndX=54.25 EndY=10.75 EndZ=0
    g5: LineSegment StartX=54.25 StartY=10.75 StartZ=0 EndX=59.25 EndY=10.75 EndZ=0
    g6: LineSegment StartX=59.25 StartY=10.75 StartZ=0 EndX=59.25 EndY=13.5 EndZ=0
    g7: LineSegment StartX=59.25 StartY=13.5 StartZ=0 EndX=61.75 EndY=13.5 EndZ=0
  constraints (16):
    c: Vertical(g0)
    c: Coincident(g0,g1)
    c: Horizontal(g1)
    c: Coincident(g1,g2)
    c: Vertical(g2)
    c: Coincident(g2,g3)
    c: Horizontal(g3)
    c: Coincident(g3,g4)
    c: Vertical(g4)
    c: Coincident(g4,g5)
    c: Horizontal(g5)
    c: Coincident(g5,g6)
    c: Vertical(g6)
    c: Coincident(g6,g7)
    c: Coincident(g7,g0)
    c: Horizontal(g7)
FEATURE [PartDesign::Pad] Pad035
  BaseFeature = -> Pocket027
  Length = 2
  Length2 = 100
  Placement = pos=(157,0,0) rot=(0.57735,0.57735,0.57735;2.0944rad)
  Profile = -> Sketch062
  Reversed = true
  Type = 0
FEATURE [PartDesign::Body] Body004  label="Switch"
  Group = -> [Sketch056,Pad031,Sketch057,Pocket027,Sketch062,Pad035]
  Origin = -> Origin004
  Tip = -> Pad035
FEATURE [Sketcher::SketchObject] Sketch063
  MapMode = 5
  Placement = pos=(0,0,30) rot=(1,0,0;3.14159rad)
  sketch-geometry (1):
    g0: Circle CenterX=14.5 CenterY=-4 CenterZ=0 NormalX=0 NormalY=0 NormalZ=1 AngleXU=0 Radius=6.5
FEATURE [PartDesign::Pad] Pad036
  Length = 6
  Length2 = 100
  Placement = pos=(0,0,30) rot=(1,0,0;3.14159rad)
  Profile = -> Sketch063
  Reversed = true
  Type = 0
FEATURE [PartDesign::Chamfer] Chamfer002
  Base = -> Pad036 [Edge3]
  BaseFeature = -> Pad036
  Placement = pos=(0,0,30) rot=(1,0,0;3.14159rad)
  Size = 1
FEATURE [Sketcher::SketchObject] Sketch064
  MapMode = 5
  Placement = pos=(0,0,32) rot=(0,0,1;0rad)
  Support = -> [Pocket028]
  sketch-geometry (1):
    g0: Circle CenterX=14.5 CenterY=6 CenterZ=0 NormalX=0 NormalY=0 NormalZ=1 AngleXU=0 Radius=5.5
FEATURE [Sketcher::SketchObject] Sketch065
  MapMode = 5
  Placement = pos=(0,0,32) rot=(0,0,1;0rad)
  Support = -> [Pocket028]
  sketch-geometry (1):
    g0: Circle CenterX=14.5 CenterY=4 CenterZ=0 NormalX=0 NormalY=0 NormalZ=1 AngleXU=0 Radius=5.5
FEATURE [PartDesign::Pad] Pad037
  BaseFeature = -> Pocket028
  Length = 2
  Length2 = 100
  Profile = -> Sketch065
  Reversed = true
  Type = 0
FEATURE [PartDesign::Pocket] Pocket029
  BaseFeature = -> Pad037
  Length = 5
  Length2 = 100
  Profile = -> Sketch064
  Type = 0
FEATURE [Sketcher::SketchObject] Sketch066
  MapMode = 5
  Placement = pos=(0,0,30) rot=(1,0,0;3.14159rad)
  Support = -> [Chamfer002]
  sketch-geometry (1):
    g0: Circle CenterX=14.5 CenterY=-4 CenterZ=0 NormalX=0 NormalY=0 NormalZ=1 AngleXU=0 Radius=4
FEATURE [PartDesign::Pad] Pad038
  BaseFeature = -> Chamfer002
  Length = 12.5
  Length2 = 100
  Placement = pos=(0,0,30) rot=(1,0,0;3.14159rad)
  Profile = -> Sketch066
  Type = 0
FEATURE [Sketcher::SketchObject] Sketch067
  AttachmentOffset = pos=(0,0,-4) rot=(0,0,1;0rad)
  MapMode = 5
  Placement = pos=(0,0,17.5) rot=(1,0,0;3.14159rad)
  Support = -> [Pad038]
  sketch-geometry (4):
    g0: ArcOfCircle CenterX=14.5 CenterY=-3.96728 CenterZ=0 NormalX=0 NormalY=0 NormalZ=1 AngleXU=0 Radius=3.29577 StartAngle=2.7147 EndAngle=6.71008
    g1: LineSegment [constr] StartX=14.5 StartY=-7.26305 StartZ=0 EndX=14.5 EndY=-2.6027 EndZ=0
    g2: LineSegment StartX=14.5 StartY=-2.6027 StartZ=0 EndX=17.5 EndY=-2.6027 EndZ=0
    g3: LineSegment StartX=14.5 StartY=-2.6027 StartZ=0 EndX=11.5 EndY=-2.6027 EndZ=0
  constraints (8):
    c: PointOnObject(g1,g0)
    c: Vertical(g1)
    c: Coincident(g2,g1)
    c: Horizontal(g2)
    c: Coincident(g3,g1)
    c: Horizontal(g3)
    c: PointOnObject(g0,g3)
    c: PointOnObject(g0,g2)
FEATURE [PartDesign::Pocket] Pocket030
  BaseFeature = -> Pad038
  Length = 7
  Length2 = 100
  Placement = pos=(0,0,30) rot=(1,0,0;3.14159rad)
  Profile = -> Sketch067
  Type = 0
FEATURE [PartDesign::Body] Body005  label="Volume"
  Group = -> [Sketch063,Pad036,Chamfer002,Sketch066,Pad038,Sketch067,Pocket030]
  Origin = -> Origin005
  Placement = pos=(0,2,2.5) rot=(0,0,1;0rad)
  Tip = -> Pocket030
FEATURE [Sketcher::SketchObject] Sketch069
  MapMode = 5
  Placement = pos=(0,0,32) rot=(0,0,1;0rad)
  sketch-geometry (1):
    g0: Circle CenterX=5.5 CenterY=-22.5 CenterZ=0 NormalX=0 NormalY=0 NormalZ=1 AngleXU=0 Radius=3
FEATURE [PartDesign::Pad] Pad040
  Length = 0.5
  Length2 = 100
  Placement = pos=(0,0,32) rot=(0,0,1;0rad)
  Profile = -> Sketch069
  Type = 0
FEATURE [Sketcher::SketchObject] Sketch070
  MapMode = 5
  Placement = pos=(0,0,32) rot=(0,0,1;0rad)
  sketch-geometry (1):
    g0: Circle CenterX=5.5 CenterY=-22.5 CenterZ=0 NormalX=0 NormalY=0 NormalZ=1 AngleXU=0 Radius=3
FEATURE [PartDesign::Pad] Pad041
  BaseFeature = -> Pad040
  Length = 1.5
  Length2 = 100
  Placement = pos=(0,0,32) rot=(0,0,1;0rad)
  Profile = -> Sketch070
  Reversed = true
  Type = 0
FEATURE [Sketcher::SketchObject] Sketch071
  MapMode = 5
  Placement = pos=(0,0,30.5) rot=(1,0,0;3.14159rad)
  Support = -> [Pad041]
  sketch-geometry (1):
    g0: Circle CenterX=5.5 CenterY=22.5 CenterZ=0 NormalX=0 NormalY=0 NormalZ=1 AngleXU=0 Radius=2
FEATURE [Sketcher::SketchObject] Sketch072
  MapMode = 5
  Placement = pos=(0,0,32.5) rot=(0,0,1;0rad)
  sketch-geometry (1):
    g0: Circle CenterX=5.5 CenterY=-22.5 CenterZ=0 NormalX=0 NormalY=0 NormalZ=1 AngleXU=0 Radius=8
FEATURE [Sketcher::SketchObject] Sketch073
  MapMode = 5
  Placement = pos=(0,0,25) rot=(1,0,0;3.14159rad)
  sketch-geometry (1):
    g0: Circle CenterX=5.5 CenterY=22.5 CenterZ=0 NormalX=0 NormalY=0 NormalZ=1 AngleXU=0 Radius=1.69883
FEATURE [PartDesign::Pad] Pad043
  Length = 4
  Length2 = 100
  Placement = pos=(0,0,25) rot=(1,0,0;3.14159rad)
  Profile = -> Sketch073
  Reversed = true
  Type = 0
FEATURE [Sketcher::SketchObject] Sketch074
  MapMode = 5
  Placement = pos=(0,0,25) rot=(1,0,0;3.14159rad)
  Support = -> [Pad043]
  sketch-geometry (4):
    g0: LineSegment StartX=-2 StartY=30 StartZ=0 EndX=13 EndY=30 EndZ=0
    g1: LineSegment StartX=13 StartY=30 StartZ=0 EndX=13 EndY=15 EndZ=0
    g2: LineSegment StartX=13 StartY=15 StartZ=0 EndX=-2 EndY=15 EndZ=0
    g3: LineSegment StartX=-2 StartY=15 StartZ=0 EndX=-2 EndY=30 EndZ=0
  constraints (8):
    c: Coincident(g0,g1)
    c: Coincident(g1,g2)
    c: Coincident(g2,g3)
    c: Coincident(g3,g0)
    c: Horizontal(g0)
    c: Horizontal(g2)
    c: Vertical(g1)
    c: Vertical(g3)
FEATURE [PartDesign::Pad] Pad044
  BaseFeature = -> Pad043
  Length = 6.5
  Length2 = 100
  Placement = pos=(0,0,25) rot=(1,0,0;3.14159rad)
  Profile = -> Sketch074
  Type = 0
FEATURE [Sketcher::SketchObject] Sketch078
  MapMode = 5
  Placement = pos=(0,1e-15,18.5) rot=(1,0,0;3.14159rad)
  sketch-geometry (4):
    g0: LineSegment StartX=3.5 StartY=24.5 StartZ=0 EndX=7.5 EndY=24.5 EndZ=0
    g1: LineSegment StartX=7.5 StartY=24.5 StartZ=0 EndX=7.5 EndY=20.5 EndZ=0
    g2: LineSegment StartX=7.5 StartY=20.5 StartZ=0 EndX=3.5 EndY=20.5 EndZ=0
    g3: LineSegment StartX=3.5 StartY=20.5 StartZ=0 EndX=3.5 EndY=24.5 EndZ=0
  constraints (8):
    c: Coincident(g0,g1)
    c: Coincident(g1,g2)
    c: Coincident(g2,g3)
    c: Coincident(g3,g0)
    c: Horizontal(g0)
    c: Horizontal(g2)
    c: Vertical(g1)
    c: Vertical(g3)
FEATURE [PartDesign::Pocket] Pocket033
  BaseFeature = -> Pad044
  Length = 6
  Length2 = 100
  Placement = pos=(0,0,25) rot=(1,0,0;3.14159rad)
  Profile = -> Sketch078
  Type = 0
FEATURE [Sketcher::SketchObject] Sketch079
  MapMode = 5
  Placement = pos=(0,2e-15,22) rot=(1,0,0;3.14159rad)
  sketch-geometry (4):
    g0: LineSegment StartX=3.625 StartY=24.375 StartZ=0 EndX=7.375 EndY=24.375 EndZ=0
    g1: LineSegment StartX=7.375 StartY=24.375 StartZ=0 EndX=7.375 EndY=20.625 EndZ=0
    g2: LineSegment StartX=7.375 StartY=20.625 StartZ=0 EndX=3.625 EndY=20.625 EndZ=0
    g3: LineSegment StartX=3.625 StartY=20.625 StartZ=0 EndX=3.625 EndY=24.375 EndZ=0
  constraints (8):
    c: Coincident(g0,g1)
    c: Coincident(g1,g2)
    c: Coincident(g2,g3)
    c: Coincident(g3,g0)
    c: Horizontal(g0)
    c: Horizontal(g2)
    c: Vertical(g1)
    c: Vertical(g3)
FEATURE [PartDesign::Pad] Pad046
  Length = 4
  Length2 = 100
  Placement = pos=(0,2e-15,22) rot=(1,0,0;3.14159rad)
  Profile = -> Sketch079
  Reversed = true
  Type = 0
FEATURE [Sketcher::SketchObject] Sketch080
  MapMode = 5
  Placement = pos=(0,2e-15,22) rot=(1,0,0;3.14159rad)
  Support = -> [Pad046]
  sketch-geometry (1):
    g0: Circle CenterX=5.5 CenterY=22.5 CenterZ=0 NormalX=0 NormalY=0 NormalZ=1 AngleXU=0 Radius=3
FEATURE [PartDesign::Pad] Pad047
  BaseFeature = -> Pad046
  Length = 3
  Length2 = 100
  Placement = pos=(0,2e-15,22) rot=(1,0,0;3.14159rad)
  Profile = -> Sketch080
  Type = 0
FEATURE [Sketcher::SketchObject] Sketch081
  MapMode = 5
  Placement = pos=(0,2e-15,19) rot=(1,0,0;3.14159rad)
  Support = -> [Pad047]
  sketch-geometry (4):
    g0: LineSegment StartX=4.375 StartY=23.625 StartZ=0 EndX=6.625 EndY=23.625 EndZ=0
    g1: LineSegment StartX=6.625 StartY=23.625 StartZ=0 EndX=6.625 EndY=21.375 EndZ=0
    g2: LineSegment StartX=6.625 StartY=21.375 StartZ=0 EndX=4.375 EndY=21.375 EndZ=0
    g3: LineSegment StartX=4.375 StartY=21.375 StartZ=0 EndX=4.375 EndY=23.625 EndZ=0
  constraints (8):
    c: Coincident(g0,g1)
    c: Coincident(g1,g2)
    c: Coincident(g2,g3)
    c: Coincident(g3,g0)
    c: Horizontal(g0)
    c: Horizontal(g2)
    c: Vertical(g1)
    c: Vertical(g3)
FEATURE [PartDesign::Pocket] Pocket034
  BaseFeature = -> Pad047
  Length = 3
  Length2 = 100
  Placement = pos=(0,2e-15,22) rot=(1,0,0;3.14159rad)
  Profile = -> Sketch081
  Type = 0
FEATURE [Sketcher::SketchObject] Sketch082
  MapMode = 5
  Placement = pos=(0,0,18.5) rot=(1,0,0;3.14159rad)
  sketch-geometry (2):
    g0: Circle CenterX=5.5 CenterY=22.5 CenterZ=0 NormalX=0 NormalY=0 NormalZ=1 AngleXU=0 Radius=2.12132
    g1: Circle CenterX=5.5 CenterY=22.5 CenterZ=0 NormalX=0 NormalY=0 NormalZ=1 AngleXU=0 Radius=3.53553
  constraints (1):
    c: Coincident(g1,g0)
FEATURE [PartDesign::Fillet] Fillet006
  Base = -> Pocket033 [Edge2,Edge8,Edge5,Edge1]
  BaseFeature = -> Pocket033
  Placement = pos=(0,0,25) rot=(1,0,0;3.14159rad)
  Radius = 1
FEATURE [PartDesign::Pad] Pad049
  BaseFeature = -> Pad041
  Length = 2
  Length2 = 100
  Placement = pos=(0,0,32) rot=(0,0,1;0rad)
  Profile = -> Sketch072
  Type = 0
FEATURE [PartDesign::Fillet] Fillet008
  Base = -> Pocket029 [Edge36,Edge333]
  BaseFeature = -> Pocket029
  Radius = 3
FEATURE [Sketcher::SketchObject] Sketch083
  MapMode = 5
  Placement = pos=(0,0,2) rot=(1,0,0;3.14159rad)
  Support = -> [Fillet008]
  sketch-geometry (16):
    g0: LineSegment StartX=0 StartY=66 StartZ=0 EndX=145 EndY=66 EndZ=0
    g1: LineSegment StartX=145 StartY=66 StartZ=0 EndX=145 EndY=64 EndZ=0
    g2: LineSegment StartX=145 StartY=64 StartZ=0 EndX=0 EndY=64 EndZ=0
    g3: LineSegment StartX=0 StartY=64 StartZ=0 EndX=0 EndY=66 EndZ=0
    g4: LineSegment StartX=-5 StartY=59 StartZ=0 EndX=-7 EndY=59 EndZ=0
    g5: LineSegment StartX=-7 StartY=59 StartZ=0 EndX=-7 EndY=-10 EndZ=0
    g6: LineSegment StartX=-7 StartY=-10 StartZ=0 EndX=-5 EndY=-10 EndZ=0
    g7: LineSegment StartX=-5 StartY=-10 StartZ=0 EndX=-5 EndY=59 EndZ=0
    g8: LineSegment StartX=0 StartY=-15 StartZ=0 EndX=144 EndY=-15 EndZ=0
    g9: LineSegment StartX=144 StartY=-15 StartZ=0 EndX=144 EndY=-17 EndZ=0
    g10: LineSegment StartX=144 StartY=-17 StartZ=0 EndX=0 EndY=-17 EndZ=0
    g11: LineSegment StartX=0 StartY=-17 StartZ=0 EndX=0 EndY=-15 EndZ=0
    g12: LineSegment StartX=151 StartY=59 StartZ=0 EndX=149 EndY=59 EndZ=0
    g13: LineSegment StartX=149 StartY=59 StartZ=0 EndX=149 EndY=-11 EndZ=0
    g14: LineSegment StartX=149 StartY=-11 StartZ=0 EndX=151 EndY=-11 EndZ=0
    g15: LineSegment StartX=151 StartY=-11 StartZ=0 EndX=151 EndY=59 EndZ=0
  constraints (33):
    c: Coincident(g0,g1)
    c: Coincident(g1,g2)
    c: Coincident(g2,g3)
    c: Coincident(g3,g0)
    c: Horizontal(g0)
    c: Horizontal(g2)
    c: Vertical(g1)
    c: Vertical(g3)
    c: Coincident(g4,g5)
    c: Coincident(g5,g6)
    c: Coincident(g6,g7)
    c: Coincident(g7,g4)
    c: Horizontal(g4)
    c: Horizontal(g6)
    c: Vertical(g5)
    c: Vertical(g7)
    c: Coincident(g8,g9)
    c: Coincident(g9,g10)
    c: Coincident(g10,g11)
    c: Coincident(g11,g8)
    c: Horizontal(g8)
    c: Horizontal(g10)
    c: Vertical(g9)
    c: Vertical(g11)
    c: PointOnObject(g8,g-2)
    c: Coincident(g12,g13)
    c: Coincident(g13,g14)
    c: Coincident(g14,g15)
    c: Coincident(g15,g12)
    c: Horizontal(g12)
    c: Horizontal(g14)
    c: Vertical(g13)
    c: Vertical(g15)
FEATURE [PartDesign::Pad] Pad050
  BaseFeature = -> Fillet008
  Length = 1
  Length2 = 100
  Profile = -> Sketch083
  Reversed = true
  Type = 0
FEATURE [Sketcher::SketchObject] Sketch084
  MapMode = 5
  Placement = pos=(0,0,16) rot=(1,0,0;3.14159rad)
  Support = -> [Pad050]
  sketch-geometry (4):
    g0: LineSegment StartX=59 StartY=-2 StartZ=0 EndX=104 EndY=-2 EndZ=0
    g1: LineSegment StartX=104 StartY=-2 StartZ=0 EndX=104 EndY=-3 EndZ=0
    g2: LineSegment StartX=104 StartY=-3 StartZ=0 EndX=59 EndY=-3 EndZ=0
    g3: LineSegment StartX=59 StartY=-3 StartZ=0 EndX=59 EndY=-2 EndZ=0
  constraints (8):
    c: Coincident(g0,g1)
    c: Coincident(g1,g2)
    c: Coincident(g2,g3)
    c: Coincident(g3,g0)
    c: Horizontal(g0)
    c: Horizontal(g2)
    c: Vertical(g1)
    c: Vertical(g3)
FEATURE [PartDesign::Pocket] Pocket036
  BaseFeature = -> Pad050
  Length = 14
  Length2 = 100
  Offset = 1
  Profile = -> Sketch084
  Type = 0
FEATURE [PartDesign::Body] Body  label="Krabicka"
  Group = -> [Sketch,Pad,Sketch001,Sketch002,Sketch003,Pocket,Pocket001,Sketch004,Pocket002,Sketch005,Pad001,Sketch007,Pad002,Sketch008,Pocket003,Sketch009,Pad003,Sketch010,Pocket004,Sketch011,Pocket005,Sketch012,Pad004,Sketch013,Pocket006,Sketch014,Pad005,Sketch016,Pad006,Sketch017,Sketch018,Sketch019,Sketch020,Sketch021,Pocket011,Pocket012,Pad007,Pocket013,Pocket014,Sketch022,Pocket015,Sketch023,Pocket022,+42 more]
  Origin = -> Origin
  Tip = -> Pocket036
FEATURE [Sketcher::SketchObject] Sketch050
  MapMode = 5
  Placement = pos=(-2e-15,3e-15,26) rot=(1,0,0;3.14159rad)
  Support = -> [Pad025]
  sketch-geometry (1):
    g0: Circle CenterX=101 CenterY=55 CenterZ=0 NormalX=0 NormalY=0 NormalZ=1 AngleXU=0 Radius=1.5
FEATURE [PartDesign::Pocket] Pocket026
  BaseFeature = -> Pad025
  Length = 4
  Length2 = 100
  Placement = pos=(0,0,30) rot=(1,0,0;3.14159rad)
  Profile = -> Sketch050
  Type = 0
FEATURE [PartDesign::Body] Body002  label="Tlacitko_horni_base"
  Group = -> [Sketch046,Pad023,Sketch047,Pad024,Fillet003,Sketch049,Pad025,Sketch050,Pocket026]
  Origin = -> Origin002
  Placement = pos=(75,0,0) rot=(0,0,1;0rad)
  Tip = -> Pocket026
FEATURE [PartDesign::FeatureBase] Clone
  BaseFeature = -> Body002
  Placement = pos=(75,0,0) rot=(0,0,1;0rad)
FEATURE [PartDesign::FeatureBase] Clone001 .. Clone007  x7 (patterned run collapsed; names and placements below)
  BaseFeature = -> Body002
  placements: all 7 at pos=(75,0,0) rot=(0,0,1;0rad)
FEATURE [Sketcher::SketchObject] Sketch085
  AttachmentOffset = pos=(101,-55,0) rot=(0,0,1;0rad)
  MapMode = 5
  Placement = pos=(176,-55,35.5) rot=(0,0,1;0rad)
  Support = -> [Clone003]
  sketch-geometry (11):
    g0: LineSegment StartX=-0.6 StartY=-2.6 StartZ=0 EndX=-0.6 EndY=-1 EndZ=0
    g1: LineSegment StartX=-0.6 StartY=-1 StartZ=0 EndX=0.6 EndY=-1 EndZ=0
    g2: LineSegment StartX=0.6 StartY=-1 StartZ=0 EndX=0.6 EndY=-2.6 EndZ=0
    g3: LineSegment StartX=0.6 StartY=-2.6 StartZ=0 EndX=2.2 EndY=-2.6 EndZ=0
    g4: LineSegment StartX=2.2 StartY=-2.6 StartZ=0 EndX=2.2 EndY=0.2 EndZ=0
    g5: LineSegment StartX=2.2 StartY=0.2 StartZ=0 EndX=3.2 EndY=0.2 EndZ=0
    g6: LineSegment StartX=3.2 StartY=0.2 StartZ=0 EndX=0 EndY=3.4 EndZ=0
    g7: LineSegment StartX=-0.6 StartY=-2.6 StartZ=0 EndX=-2.2 EndY=-2.6 EndZ=0
    g8: LineSegment StartX=-2.2 StartY=-2.6 StartZ=0 EndX=-2.2 EndY=0.2 EndZ=0
    g9: LineSegment StartX=-2.2 StartY=0.2 StartZ=0 EndX=-3.2 EndY=0.2 EndZ=0
    g10: LineSegment StartX=-3.2 StartY=0.2 StartZ=0 EndX=0 EndY=3.4 EndZ=0
  constraints (20):
    c: Vertical(g0)
    c: Coincident(g0,g1)
    c: Horizontal(g1)
    c: Coincident(g1,g2)
    c: Vertical(g2)
    c: Coincident(g2,g3)
    c: Horizontal(g3)
    c: Coincident(g3,g4)
    c: Vertical(g4)
    c: Coincident(g4,g5)
    c: Horizontal(g5)
    c: Coincident(g5,g6)
    c: Horizontal(g7)
    c: Coincident(g7,g8)
    c: Vertical(g8)
    c: Coincident(g8,g9)
    c: Horizontal(g9)
    c: Coincident(g9,g10)
    c: Coincident(g6,g10)
    c: Coincident(g0,g7)
FEATURE [Sketcher::SketchObject] Sketch086
  AttachmentOffset = pos=(101,-55,0) rot=(0,0,1;0rad)
  MapMode = 5
  Placement = pos=(176,-55,35.5) rot=(0,0,1;0rad)
  Support = -> [Clone001]
  sketch-geometry (4):
    g0: LineSegment StartX=1.8 StartY=0.3 StartZ=0 EndX=1.8 EndY=-0.3 EndZ=0
    g1: LineSegment StartX=1.8 StartY=0.3 StartZ=0 EndX=3 EndY=0.3 EndZ=0
    g2: LineSegment StartX=1.8 StartY=-0.3 StartZ=0 EndX=3 EndY=-0.3 EndZ=0
    g3: ArcOfCircle CenterX=3 CenterY=0 CenterZ=0 NormalX=0 NormalY=0 NormalZ=1 AngleXU=0 Radius=0.3 StartAngle=4.71239 EndAngle=7.85398
  constraints (8):
    c: Vertical(g0)
    c: Coincident(g0,g1)
    c: Horizontal(g1)
    c: Coincident(g0,g2)
    c: Horizontal(g2)
    c: PointOnObject(g3,g-1)
    c: Coincident(g3,g1)
    c: Coincident(g3,g2)
FEATURE [Sketcher::SketchObject] Sketch087
  AttachmentOffset = pos=(101,-55,0) rot=(0,0,1;0rad)
  MapMode = 5
  Placement = pos=(176,-55,35.5) rot=(0,0,1;0rad)
  Support = -> [Clone001]
  sketch-geometry (2):
    g0: Circle CenterX=0 CenterY=0 CenterZ=0 NormalX=0 NormalY=0 NormalZ=1 AngleXU=0 Radius=1
    g1: Circle CenterX=0 CenterY=0 CenterZ=0 NormalX=0 NormalY=0 NormalZ=1 AngleXU=0 Radius=1.5
  constraints (2):
    c: Coincident(g0,g-1)
    c: Coincident(g1,g0)
FEATURE [Sketcher::SketchObject] Sketch088
  MapMode = 5
  Placement = pos=(75,0,35.5) rot=(0,0,1;0rad)
  Support = -> [Clone001]
  sketch-geometry (8):
    g0: LineSegment StartX=100.5 StartY=-52.5 StartZ=0 EndX=99 EndY=-52.5 EndZ=0
    g1: LineSegment StartX=99 StartY=-52.5 StartZ=0 EndX=99 EndY=-57.5 EndZ=0
    g2: LineSegment StartX=99 StartY=-57.5 StartZ=0 EndX=100.5 EndY=-57.5 EndZ=0
    g3: LineSegment StartX=100.5 StartY=-57.5 StartZ=0 EndX=100.5 EndY=-52.5 EndZ=0
    g4: LineSegment StartX=103 StartY=-52.5 StartZ=0 EndX=101.5 EndY=-52.5 EndZ=0
    g5: LineSegment StartX=101.5 StartY=-52.5 StartZ=0 EndX=101.5 EndY=-57.5 EndZ=0
    g6: LineSegment StartX=101.5 StartY=-57.5 StartZ=0 EndX=103 EndY=-57.5 EndZ=0
    g7: LineSegment StartX=103 StartY=-57.5 StartZ=0 EndX=103 EndY=-52.5 EndZ=0
  constraints (16):
    c: Coincident(g0,g1)
    c: Coincident(g1,g2)
    c: Coincident(g2,g3)
    c: Coincident(g3,g0)
    c: Horizontal(g0)
    c: Horizontal(g2)
    c: Vertical(g1)
    c: Vertical(g3)
    c: Coincident(g4,g5)
    c: Coincident(g5,g6)
    c: Coincident(g6,g7)
    c: Coincident(g7,g4)
    c: Horizontal(g4)
    c: Horizontal(g6)
    c: Vertical(g5)
    c: Vertical(g7)
FEATURE [Sketcher::SketchObject] Sketch089
  AttachmentOffset = pos=(101,-55,0) rot=(0,0,1;0rad)
  MapMode = 5
  Placement = pos=(176,-55,35.5) rot=(0,0,1;0rad)
  Support = -> [Clone]
  sketch-geometry (10):
    g0: LineSegment StartX=-3 StartY=1 StartZ=0 EndX=-3 EndY=-1 EndZ=0
    g1: LineSegment StartX=-3 StartY=-1 StartZ=0 EndX=-1.5 EndY=-1 EndZ=0
    g2: LineSegment StartX=-1.5 StartY=-1 StartZ=0 EndX=0.5 EndY=-2.5 EndZ=0
    g3: LineSegment StartX=0.5 StartY=-2.5 StartZ=0 EndX=0.5 EndY=2.5 EndZ=0
    g4: LineSegment StartX=0.5 StartY=2.5 StartZ=0 EndX=-1.5 EndY=1 EndZ=0
    g5: LineSegment StartX=-1.5 StartY=1 StartZ=0 EndX=-3 EndY=1 EndZ=0
    g6: ArcOfCircle CenterX=0 CenterY=0 CenterZ=0 NormalX=0 NormalY=0 NormalZ=1 AngleXU=0 Radius=2.60613 StartAngle=5.37754 EndAngle=7.18884
    g7: ArcOfCircle CenterX=-0.5 CenterY=0 CenterZ=0 NormalX=0 NormalY=0 NormalZ=1 AngleXU=0 Radius=2.24406 StartAngle=5.52537 EndAngle=7.041
    g8: LineSegment StartX=1.60844 StartY=2.05057 StartZ=0 EndX=1.12995 EndY=1.54242 EndZ=0
    g9: LineSegment StartX=1.60844 StartY=-2.05057 StartZ=0 EndX=1.12995 EndY=-1.54242 EndZ=0
  constraints (16):
    c: Vertical(g0)
    c: Coincident(g0,g1)
    c: Horizontal(g1)
    c: Coincident(g1,g2)
    c: Coincident(g2,g3)
    c: Vertical(g3)
    c: Coincident(g3,g4)
    c: Coincident(g4,g5)
    c: Coincident(g5,g0)
    c: Horizontal(g5)
    c: PointOnObject(g6,g-1)
    c: PointOnObject(g7,g-1)
    c: Coincident(g8,g6)
    c: Coincident(g8,g7)
    c: Coincident(g9,g6)
    c: Coincident(g9,g7)
FEATURE [Sketcher::SketchObject] Sketch090
  MapMode = 5
  Placement = pos=(75,0,35.5) rot=(0,0,1;0rad)
  Support = -> [Clone004]
  sketch-geometry (6):
    g0: LineSegment StartX=98.5 StartY=-56.5 StartZ=0 EndX=103.5 EndY=-56.5 EndZ=0
    g1: LineSegment StartX=103.5 StartY=-56.5 StartZ=0 EndX=101 EndY=-52.5 EndZ=0
    g2: LineSegment StartX=101 StartY=-52.5 StartZ=0 EndX=98.5 EndY=-56.5 EndZ=0
    g3: LineSegment StartX=101 StartY=-53.5 StartZ=0 EndX=99.5 EndY=-56 EndZ=0
    g4: LineSegment StartX=99.5 StartY=-56 StartZ=0 EndX=102.5 EndY=-56 EndZ=0
    g5: LineSegment StartX=102.5 StartY=-56 StartZ=0 EndX=101 EndY=-53.5 EndZ=0
  constraints (8):
    c: Horizontal(g0)
    c: Coincident(g0,g1)
    c: Coincident(g1,g2)
    c: Coincident(g2,g0)
    c: Coincident(g3,g4)
    c: Horizontal(g4)
    c: Coincident(g4,g5)
    c: Coincident(g5,g3)
FEATURE [Sketcher::SketchObject] Sketch091
  MapMode = 5
  Placement = pos=(75,0,35.5) rot=(0,0,1;0rad)
  Support = -> [Clone005]
  sketch-geometry (8):
    g0: LineSegment StartX=99 StartY=-53 StartZ=0 EndX=99 EndY=-57 EndZ=0
    g1: LineSegment StartX=99 StartY=-57 StartZ=0 EndX=103 EndY=-57 EndZ=0
    g2: LineSegment StartX=103 StartY=-57 StartZ=0 EndX=103 EndY=-53 EndZ=0
    g3: LineSegment StartX=103 StartY=-53 StartZ=0 EndX=99 EndY=-53 EndZ=0
    g4: LineSegment StartX=99.5 StartY=-53.5 StartZ=0 EndX=99.5 EndY=-56.5 EndZ=0
    g5: LineSegment StartX=99.5 StartY=-56.5 StartZ=0 EndX=102.5 EndY=-56.5 EndZ=0
    g6: LineSegment StartX=102.5 StartY=-56.5 StartZ=0 EndX=102.5 EndY=-53.5 EndZ=0
    g7: LineSegment StartX=102.5 StartY=-53.5 StartZ=0 EndX=99.5 EndY=-53.5 EndZ=0
  constraints (16):
    c: Vertical(g0)
    c: Coincident(g0,g1)
    c: Horizontal(g1)
    c: Coincident(g1,g2)
    c: Vertical(g2)
    c: Coincident(g2,g3)
    c: Coincident(g3,g0)
    c: Horizontal(g3)
    c: Vertical(g4)
    c: Coincident(g4,g5)
    c: Horizontal(g5)
    c: Coincident(g5,g6)
    c: Vertical(g6)
    c: Coincident(g6,g7)
    c: Coincident(g7,g4)
    c: Horizontal(g7)
FEATURE [Sketcher::SketchObject] Sketch092
  MapMode = 5
  Placement = pos=(75,0,35.5) rot=(0,0,1;0rad)
  Support = -> [Clone006]
  sketch-geometry (2):
    g0: Circle CenterX=101 CenterY=-55 CenterZ=0 NormalX=0 NormalY=0 NormalZ=1 AngleXU=0 Radius=2.5
    g1: Circle CenterX=101 CenterY=-55 CenterZ=0 NormalX=0 NormalY=0 NormalZ=1 AngleXU=0 Radius=2
  constraints (1):
    c: Coincident(g1,g0)
FEATURE [Sketcher::SketchObject] Sketch093
  MapMode = 5
  Placement = pos=(75,0,35.5) rot=(0,0,1;0rad)
  Support = -> [Clone007]
  sketch-geometry (16):
    g0: LineSegment [constr] StartX=101 StartY=-55 StartZ=0 EndX=99 EndY=-53 EndZ=0
    g1: LineSegment [constr] StartX=101 StartY=-55 StartZ=0 EndX=103 EndY=-57 EndZ=0
    g2: LineSegment [constr] StartX=101 StartY=-55 StartZ=0 EndX=103 EndY=-53 EndZ=0
    g3: LineSegment [constr] StartX=101 StartY=-55 StartZ=0 EndX=99 EndY=-57 EndZ=0
    g4: LineSegment StartX=99.5 StartY=-53 StartZ=0 EndX=99 EndY=-53.5 EndZ=0
    g5: LineSegment StartX=99 StartY=-53.5 StartZ=0 EndX=100.5 EndY=-55 EndZ=0
    g6: LineSegment StartX=100.5 StartY=-55 StartZ=0 EndX=99 EndY=-56.5 EndZ=0
    g7: LineSegment StartX=99 StartY=-56.5 StartZ=0 EndX=99.5 EndY=-57 EndZ=0
    g8: LineSegment StartX=99.5 StartY=-57 StartZ=0 EndX=101 EndY=-55.5 EndZ=0
    g9: LineSegment StartX=101 StartY=-55.5 StartZ=0 EndX=102.5 EndY=-57 EndZ=0
    g10: LineSegment StartX=102.5 StartY=-57 StartZ=0 EndX=103 EndY=-56.5 EndZ=0
    g11: LineSegment StartX=103 StartY=-56.5 StartZ=0 EndX=101.5 EndY=-55 EndZ=0
    g12: LineSegment StartX=101.5 StartY=-55 StartZ=0 EndX=103 EndY=-53.5 EndZ=0
    g13: LineSegment StartX=103 StartY=-53.5 StartZ=0 EndX=102.5 EndY=-53 EndZ=0
    g14: LineSegment StartX=102.5 StartY=-53 StartZ=0 EndX=101 EndY=-54.5 EndZ=0
    g15: LineSegment StartX=101 StartY=-54.5 StartZ=0 EndX=99.5 EndY=-53 EndZ=0
  constraints (14):
    c: Coincident(g2,g0)
    c: Coincident(g3,g0)
    c: Coincident(g4,g5)
    c: Coincident(g5,g6)
    c: Coincident(g6,g7)
    c: Coincident(g7,g8)
    c: Coincident(g8,g9)
    c: Coincident(g9,g10)
    c: Coincident(g10,g11)
    c: Coincident(g11,g12)
    c: Coincident(g12,g13)
    c: Coincident(g13,g14)
    c: Coincident(g14,g15)
    c: Coincident(g15,g4)
FEATURE [Sketcher::SketchObject] Sketch094
  AttachmentOffset = pos=(5.5,18,22.5) rot=(0,0,1;0rad)
  MapMode = 5
  Placement = pos=(5.5,-22.5,18) rot=(1,0,0;1.5708rad)
  Support = -> [XZ_Plane006]
  sketch-geometry (9):
    g0: LineSegment StartX=0 StartY=18 StartZ=0 EndX=0 EndY=16.4802 EndZ=0
    g1: LineSegment StartX=0 StartY=16.4802 StartZ=0 EndX=8 EndY=16.4802 EndZ=0
    g2-g5: Circle [constr] x4 (B-spline internal-alignment scaffolding for g6; pole/knot coordinates omitted)
    g6: BSplineCurve PolesCount=4 KnotsCount=2 Degree=3 IsPeriodic=0
    g7: GeomPoint [constr] X=0 Y=18 Z=0
    g8: GeomPoint [constr] X=8 Y=16.4802 Z=0
  constraints (13):
    c: PointOnObject(g0,g-2)
    c: Vertical(g0)
    c: Coincident(g1,g0)
    c: Horizontal(g1)
    c: Coincident(g6,g0)
    c: Radius(g2) = 0.3
    c: Equal(g2,g3)
    c: Equal(g2,g4)
    c: Equal(g2,g5)
    c: Coincident(g6,g1)
    c: InternalAlignment(g2-g5 -> g6) x4
    c: InternalAlignment(g7,g6)
    c: InternalAlignment(g8,g6)
FEATURE [PartDesign::Revolution] Revolution
  Angle = 360
  Axis = (0,-2e-16,1)
  Base = (5.5,-22.5,18)
  BaseFeature = -> Pad049
  Placement = pos=(0,0,32) rot=(0,0,1;0rad)
  Profile = -> Sketch094
  ReferenceAxis = -> Sketch094 [V_Axis]
  Reversed = true
FEATURE [PartDesign::Pocket] Pocket046
  BaseFeature = -> Revolution
  Length = 4
  Length2 = 100
  Placement = pos=(0,0,32) rot=(0,0,1;0rad)
  Profile = -> Sketch071
  Type = 0
FEATURE [PartDesign::Body] Body006  label="Joystick_up"
  Group = -> [Sketch069,Pad040,Sketch070,Pad041,Sketch071,Sketch072,Pad049,Sketch094,Revolution,Pocket046]
  Origin = -> Origin006
  Tip = -> Pocket046
FEATURE [PartDesign::Pad] Pad051
  BaseFeature = -> Clone
  Length = 0.2
  Length2 = 100
  Placement = pos=(75,0,0) rot=(0,0,1;0rad)
  Profile = -> Sketch085
  Type = 0
FEATURE [PartDesign::Body] Body009  label="tlacitko domu"
  BaseFeature = -> Body002
  Group = -> [Clone,Sketch085,Pad051]
  Origin = -> Origin009
  Placement = pos=(-160.5,0,0) rot=(0,0,1;0rad)
  Tip = -> Pad051
FEATURE [PartDesign::Pad] Pad052
  BaseFeature = -> Clone001
  Length = 0.2
  Length2 = 100
  Placement = pos=(75,0,0) rot=(0,0,1;0rad)
  Profile = -> Sketch088
  Type = 0
FEATURE [PartDesign::Body] Body010  label="tlacitko pause"
  BaseFeature = -> Body002
  Group = -> [Clone001,Sketch088,Pad052]
  Origin = -> Origin010
  Placement = pos=(-145.5,0,0) rot=(0,0,1;0rad)
  Tip = -> Pad052
FEATURE [PartDesign::Pad] Pad053
  BaseFeature = -> Clone002
  Length = 0.2
  Length2 = 100
  Placement = pos=(75,0,0) rot=(0,0,1;0rad)
  Profile = -> Sketch086
  Type = 0
FEATURE [PartDesign::Pad] Pad054
  BaseFeature = -> Pad053
  Length = 0.2
  Length2 = 100
  Placement = pos=(75,0,0) rot=(0,0,1;0rad)
  Profile = -> Sketch087
  Type = 0
FEATURE [PartDesign::PolarPattern] PolarPattern
  Angle = 360
  Axis = -> Sketch086 [N_Axis]
  BaseFeature = -> Pad054
  Occurrences = 8
  Originals = -> [Pad053]
  Placement = pos=(75,0,0) rot=(0,0,1;0rad)
FEATURE [PartDesign::Body] Body011  label="tlacitko jas"
  BaseFeature = -> Body002
  Group = -> [Clone002,Sketch086,Sketch087,Pad053,Pad054,PolarPattern]
  Origin = -> Origin011
  Placement = pos=(-89,0,0) rot=(0,0,1;0rad)
  Tip = -> PolarPattern
FEATURE [PartDesign::Pad] Pad055
  BaseFeature = -> Clone003
  Length = 0.2
  Length2 = 100
  Placement = pos=(75,0,0) rot=(0,0,1;0rad)
  Profile = -> Sketch089
  Type = 0
FEATURE [PartDesign::Body] Body012  label="tlacitko zvuk"
  BaseFeature = -> Body002
  Group = -> [Clone003,Sketch089,Pad055]
  Origin = -> Origin012
  Placement = pos=(-75,0,0) rot=(0,0,1;0rad)
  Tip = -> Pad055
FEATURE [PartDesign::Pad] Pad056
  BaseFeature = -> Clone004
  Length = 0.2
  Length2 = 100
  Placement = pos=(75,0,0) rot=(0,0,1;0rad)
  Profile = -> Sketch090
  Type = 0
FEATURE [PartDesign::Body] Body013  label="tlacitko up"
  BaseFeature = -> Body002
  Group = -> [Clone004,Sketch090,Pad056]
  Origin = -> Origin013
  Placement = pos=(-52.5,45,0) rot=(0,0,1;0rad)
  Tip = -> Pad056
FEATURE [PartDesign::Pad] Pad057
  BaseFeature = -> Clone005
  Length = 0.2
  Length2 = 100
  Placement = pos=(75,0,0) rot=(0,0,1;0rad)
  Profile = -> Sketch091
  Type = 0
FEATURE [PartDesign::Body] Body014  label="tlacitko left"
  BaseFeature = -> Body002
  Group = -> [Clone005,Sketch091,Pad057]
  Origin = -> Origin014
  Placement = pos=(-64.5,33.5,0) rot=(0,0,1;0rad)
  Tip = -> Pad057
FEATURE [PartDesign::Pad] Pad058
  BaseFeature = -> Clone006
  Length = 0.2
  Length2 = 100
  Placement = pos=(75,0,0) rot=(0,0,1;0rad)
  Profile = -> Sketch092
  Type = 0
FEATURE [PartDesign::Body] Body015  label="tlacitko right"
  BaseFeature = -> Body002
  Group = -> [Clone006,Sketch092,Pad058]
  Origin = -> Origin015
  Placement = pos=(-40,33.5,0) rot=(0,0,1;0rad)
  Tip = -> Pad058
FEATURE [PartDesign::Pad] Pad059
  BaseFeature = -> Clone007
  Length = 0.2
  Length2 = 100
  Placement = pos=(75,0,0) rot=(0,0,1;0rad)
  Profile = -> Sketch093
  Type = 0
FEATURE [PartDesign::Body] Body016  label="tlacitko down"
  BaseFeature = -> Body002
  Group = -> [Clone007,Sketch093,Pad059]
  Origin = -> Origin016
  Placement = pos=(-52.5,22,0) rot=(0,0,1;0rad)
  Tip = -> Pad059
FEATURE [Sketcher::SketchObject] Sketch095
  MapMode = 5
  Support = -> [Pocket021]
  sketch-geometry (15):
    g0: LineSegment [constr] StartX=145 StartY=12 StartZ=0 EndX=-2 EndY=-60 EndZ=0
    g1: LineSegment [constr] StartX=-1 StartY=12 StartZ=0 EndX=146 EndY=-60 EndZ=0
    g2: GeomPoint X=72 Y=-23.7551 Z=0
    g3: LineSegment [constr] StartX=72 StartY=-23.7551 StartZ=0 EndX=1.224 EndY=-23.7551 EndZ=0
    g4: LineSegment [constr] StartX=72 StartY=-23.7551 StartZ=0 EndX=145 EndY=-23.7551 EndZ=0
    g5: LineSegment StartX=1 StartY=-9 StartZ=0 EndX=145 EndY=-9 EndZ=0
    g6: LineSegment StartX=145 StartY=-9 StartZ=0 EndX=145 EndY=-39 EndZ=0
    g7: LineSegment StartX=145 StartY=-39 StartZ=0 EndX=1 EndY=-39 EndZ=0
    g8: LineSegment StartX=1 StartY=-39 StartZ=0 EndX=1 EndY=-9 EndZ=0
    g9: LineSegment [constr] StartX=72 StartY=-23.7551 StartZ=0 EndX=72 EndY=9 EndZ=0
    g10: LineSegment [constr] StartX=72 StartY=-23.7551 StartZ=0 EndX=72 EndY=-58 EndZ=0
    g11: LineSegment StartX=57 StartY=-58 StartZ=0 EndX=87 EndY=-58 EndZ=0
    g12: LineSegment StartX=87 StartY=-58 StartZ=0 EndX=87 EndY=9 EndZ=0
    g13: LineSegment StartX=87 StartY=9 StartZ=0 EndX=57 EndY=9 EndZ=0
    g14: LineSegment StartX=57 StartY=9 StartZ=0 EndX=57 EndY=-58 EndZ=0
  constraints (25):
    c: PointOnObject(g2,g0)
    c: Coincident(g3,g2)
    c: Horizontal(g3)
    c: Coincident(g4,g2)
    c: Horizontal(g4)
    c: Coincident(g5,g6)
    c: Coincident(g6,g7)
    c: Coincident(g7,g8)
    c: Coincident(g8,g5)
    c: Horizontal(g5)
    c: Horizontal(g7)
    c: Vertical(g6)
    c: Vertical(g8)
    c: Coincident(g9,g2)
    c: Vertical(g9)
    c: Coincident(g10,g2)
    c: Vertical(g10)
    c: Coincident(g11,g12)
    c: Coincident(g12,g13)
    c: Coincident(g13,g14)
    c: Coincident(g14,g11)
    c: Horizontal(g11)
    c: Horizontal(g13)
    c: Vertical(g12)
    c: Vertical(g14)
FEATURE [PartDesign::Pad] Pad060
  BaseFeature = -> Pocket021
  Length = 5
  Length2 = 100
  Profile = -> Sketch095
  Type = 0
FEATURE [PartDesign::Body] Body001  label="Zada"
  Group = -> [Sketch029,Sketch030,Pad009,Pocket021,Sketch095,Pad060]
  Origin = -> Origin001
  Placement = pos=(0,0,2.25) rot=(0,0,1;0rad)
  Tip = -> Pad060
FEATURE [Sketcher::SketchObject] Sketch096
  MapMode = 5
  Placement = pos=(0,0,18.5) rot=(1,0,0;3.14159rad)
  Support = -> [Fillet006]
  sketch-geometry (16):
    g0: LineSegment StartX=3 StartY=27 StartZ=0 EndX=8 EndY=27 EndZ=0
    g1: LineSegment StartX=8 StartY=27 StartZ=0 EndX=9 EndY=30 EndZ=0
    g2: LineSegment StartX=9 StartY=30 StartZ=0 EndX=2 EndY=30 EndZ=0
    g3: LineSegment StartX=2 StartY=30 StartZ=0 EndX=3 EndY=27 EndZ=0
    g4: LineSegment StartX=1 StartY=25 StartZ=0 EndX=-2 EndY=26 EndZ=0
    g5: LineSegment StartX=-2 StartY=26 StartZ=0 EndX=-2 EndY=19 EndZ=0
    g6: LineSegment StartX=-2 StartY=19 StartZ=0 EndX=1 EndY=20 EndZ=0
    g7: LineSegment StartX=1 StartY=20 StartZ=0 EndX=1 EndY=25 EndZ=0
    g8: LineSegment StartX=3 StartY=18 StartZ=0 EndX=2 EndY=15 EndZ=0
    g9: LineSegment StartX=2 StartY=15 StartZ=0 EndX=9 EndY=15 EndZ=0
    g10: LineSegment StartX=9 StartY=15 StartZ=0 EndX=8 EndY=18 EndZ=0
    g11: LineSegment StartX=8 StartY=18 StartZ=0 EndX=3 EndY=18 EndZ=0
    g12: LineSegment StartX=10 StartY=25 StartZ=0 EndX=13 EndY=26 EndZ=0
    g13: LineSegment StartX=13 StartY=26 StartZ=0 EndX=13 EndY=19 EndZ=0
    g14: LineSegment StartX=13 StartY=19 StartZ=0 EndX=10 EndY=20 EndZ=0
    g15: LineSegment StartX=10 StartY=20 StartZ=0 EndX=10 EndY=25 EndZ=0
  constraints (24):
    c: Horizontal(g0)
    c: Coincident(g0,g1)
    c: Coincident(g1,g2)
    c: Horizontal(g2)
    c: Coincident(g2,g3)
    c: Coincident(g3,g0)
    c: Coincident(g4,g5)
    c: Vertical(g5)
    c: Coincident(g5,g6)
    c: Coincident(g6,g7)
    c: Coincident(g7,g4)
    c: Vertical(g7)
    c: Coincident(g8,g9)
    c: Horizontal(g9)
    c: Coincident(g9,g10)
    c: Coincident(g10,g11)
    c: Coincident(g11,g8)
    c: Horizontal(g11)
    c: Coincident(g12,g13)
    c: Vertical(g13)
    c: Coincident(g13,g14)
    c: Coincident(g14,g15)
    c: Coincident(g15,g12)
    c: Vertical(g15)
FEATURE [PartDesign::Pocket] Pocket047
  BaseFeature = -> Fillet006
  Length = 7
  Length2 = 100
  Placement = pos=(0,0,25) rot=(1,0,0;3.14159rad)
  Profile = -> Sketch096
  Type = 0
FEATURE [PartDesign::Body] Body007  label="Joystick_middle_old"
  Group = -> [Sketch073,Pad043,Sketch074,Pad044,Sketch078,Pocket033,Sketch082,Fillet006,Sketch096,Pocket047]
  Origin = -> Origin007
  Placement = pos=(0,0,4) rot=(0,0,1;0rad)
  Tip = -> Pocket047
FEATURE [Sketcher::SketchObject] Sketch097
  MapMode = 5
  Placement = pos=(0,2e-15,22) rot=(0,0,1;0rad)
  Support = -> [Pocket034]
  sketch-geometry (22):
    g0: LineSegment StartX=4 StartY=-24 StartZ=0 EndX=0.5 EndY=-24 EndZ=0
    g1: LineSegment StartX=0.5 StartY=-21 StartZ=0 EndX=4 EndY=-21 EndZ=0
    g2: LineSegment StartX=4 StartY=-21 StartZ=0 EndX=4 EndY=-17.5 EndZ=0
    g3: LineSegment StartX=7 StartY=-17.5 StartZ=0 EndX=7 EndY=-21 EndZ=0
    g4: LineSegment StartX=7 StartY=-21 StartZ=0 EndX=10.5 EndY=-21 EndZ=0
    g5: LineSegment StartX=10.5 StartY=-24 StartZ=0 EndX=7 EndY=-24 EndZ=0
    g6: LineSegment StartX=7 StartY=-24 StartZ=0 EndX=7 EndY=-27.5 EndZ=0
    g7: LineSegment StartX=4 StartY=-27.5 StartZ=0 EndX=4 EndY=-24 EndZ=0
    g8: LineSegment StartX=7 StartY=-27.5 StartZ=0 EndX=8.4 EndY=-31 EndZ=0
    g9: LineSegment StartX=8.4 StartY=-31 StartZ=0 EndX=2.6 EndY=-31 EndZ=0
    g10: LineSegment [constr] StartX=5.5 StartY=-21.5 StartZ=0 EndX=5.5 EndY=-23.5 EndZ=0
    g11: LineSegment [constr] StartX=6.5 StartY=-22.5 StartZ=0 EndX=4.5 EndY=-22.5 EndZ=0
    g12: LineSegment StartX=4 StartY=-27.5 StartZ=0 EndX=2.6 EndY=-31 EndZ=0
    g13: LineSegment StartX=7 StartY=-17.5 StartZ=0 EndX=8.4 EndY=-14 EndZ=0
    g14: LineSegment StartX=4 StartY=-17.5 StartZ=0 EndX=2.6 EndY=-14 EndZ=0
    g15: LineSegment StartX=8.4 StartY=-14 StartZ=0 EndX=2.6 EndY=-14 EndZ=0
    g16: LineSegment StartX=10.5 StartY=-24 StartZ=0 EndX=14 EndY=-25.4 EndZ=0
    g17: LineSegment StartX=14 StartY=-25.4 StartZ=0 EndX=14 EndY=-19.6 EndZ=0
    g18: LineSegment StartX=10.5 StartY=-21 StartZ=0 EndX=14 EndY=-19.6 EndZ=0
    g19: LineSegment StartX=0.5 StartY=-24 StartZ=0 EndX=-3 EndY=-25.4 EndZ=0
    g20: LineSegment StartX=-3 StartY=-25.4 StartZ=0 EndX=-3 EndY=-19.6 EndZ=0
    g21: LineSegment StartX=0.5 StartY=-21 StartZ=0 EndX=-3 EndY=-19.6 EndZ=0
  constraints (32):
    c: Horizontal(g0)
    c: Horizontal(g1)
    c: Coincident(g1,g2)
    c: Vertical(g2)
    c: Vertical(g3)
    c: Coincident(g3,g4)
    c: Horizontal(g4)
    c: Horizontal(g5)
    c: Coincident(g5,g6)
    c: Vertical(g6)
    c: Vertical(g7)
    c: Coincident(g0,g7)
    c: Horizontal(g9)
    c: Vertical(g10)
    c: Horizontal(g11)
    c: Coincident(g9,g8)
    c: Coincident(g9,g12)
    c: Horizontal(g15)
    c: Coincident(g15,g13)
    c: Coincident(g15,g14)
    c: Vertical(g17)
    c: Coincident(g16,g17)
    c: Coincident(g17,g18)
    c: Vertical(g20)
    c: Coincident(g19,g20)
    c: Coincident(g20,g21)
    c: Coincident(g1,g21)
    c: Coincident(g0,g19)
    c: Coincident(g4,g18)
    c: Coincident(g5,g16)
    c: Coincident(g3,g13)
    c: Coincident(g2,g14)
FEATURE [PartDesign::Body] Body008  label="Joystick_bottom_old"
  Group = -> [Sketch079,Pad046,Sketch080,Pad047,Sketch081,Pocket034,Sketch097]
  Origin = -> Origin008
  Tip = -> Pocket034
FEATURE [Sketcher::SketchObject] Sketch098
  MapMode = 5
  Placement = pos=(0,2e-15,22) rot=(1,0,0;3.14159rad)
  sketch-geometry (4):
    g0: LineSegment StartX=5 StartY=23 StartZ=0 EndX=6 EndY=23 EndZ=0
    g1: LineSegment StartX=6 StartY=23 StartZ=0 EndX=6 EndY=22 EndZ=0
    g2: LineSegment StartX=6 StartY=22 StartZ=0 EndX=5 EndY=22 EndZ=0
    g3: LineSegment StartX=5 StartY=22 StartZ=0 EndX=5 EndY=23 EndZ=0
  constraints (8):
    c: Coincident(g0,g1)
    c: Coincident(g1,g2)
    c: Coincident(g2,g3)
    c: Coincident(g3,g0)
    c: Horizontal(g0)
    c: Horizontal(g2)
    c: Vertical(g1)
    c: Vertical(g3)
FEATURE [PartDesign::Pad] Pad061
  Length = 4
  Length2 = 100
  Placement = pos=(0,2e-15,22) rot=(1,0,0;3.14159rad)
  Profile = -> Sketch098
  Reversed = true
  Type = 0
FEATURE [Sketcher::SketchObject] Sketch099
  MapMode = 5
  Placement = pos=(0,2e-15,22) rot=(1,0,0;3.14159rad)
  Support = -> [Pad061]
  sketch-geometry (1):
    g0: Circle CenterX=5.5 CenterY=22.5 CenterZ=0 NormalX=0 NormalY=0 NormalZ=1 AngleXU=0 Radius=3
FEATURE [PartDesign::Pad] Pad062
  BaseFeature = -> Pad061
  Length = 3
  Length2 = 3
  Placement = pos=(0,2e-15,22) rot=(1,0,0;3.14159rad)
  Profile = -> Sketch099
  Type = 4
FEATURE [Sketcher::SketchObject] Sketch102
  MapMode = 5
  Placement = pos=(0,2e-15,22) rot=(0,0,1;0rad)
  sketch-geometry (1):
    g0: Circle CenterX=5.5 CenterY=-22.5 CenterZ=0 NormalX=0 NormalY=0 NormalZ=1 AngleXU=0 Radius=1.7
  constraints (1):
    c: Radius(g0) = 1.7
FEATURE [PartDesign::Pad] Pad063
  BaseFeature = -> Pad062
  Length = 8
  Length2 = 100
  Placement = pos=(0,2e-15,22) rot=(1,0,0;3.14159rad)
  Profile = -> Sketch102
  Type = 0
FEATURE [Sketcher::SketchObject] Sketch100
  MapMode = 5
  Placement = pos=(0,2e-15,19) rot=(1,0,0;3.14159rad)
  Support = -> [Pad063]
  sketch-geometry (4):
    g0: LineSegment StartX=4.375 StartY=23.625 StartZ=0 EndX=6.625 EndY=23.625 EndZ=0
    g1: LineSegment StartX=6.625 StartY=23.625 StartZ=0 EndX=6.625 EndY=21.375 EndZ=0
    g2: LineSegment StartX=6.625 StartY=21.375 StartZ=0 EndX=4.375 EndY=21.375 EndZ=0
    g3: LineSegment StartX=4.375 StartY=21.375 StartZ=0 EndX=4.375 EndY=23.625 EndZ=0
  constraints (8):
    c: Coincident(g0,g1)
    c: Coincident(g1,g2)
    c: Coincident(g2,g3)
    c: Coincident(g3,g0)
    c: Horizontal(g0)
    c: Horizontal(g2)
    c: Vertical(g1)
    c: Vertical(g3)
FEATURE [PartDesign::Pocket] Pocket048
  BaseFeature = -> Pad063
  Length = 2.5
  Length2 = 100
  Placement = pos=(0,2e-15,22) rot=(1,0,0;3.14159rad)
  Profile = -> Sketch100
  Type = 0
FEATURE [PartDesign::Body] Body017  label="Joystick_bottom"
  Group = -> [Sketch098,Pad061,Sketch099,Pad062,Sketch100,Sketch102,Pad063,Pocket048]
  Origin = -> Origin017
  Tip = -> Pocket048
FEATURE [Sketcher::SketchObject] Sketch103
  MapMode = 5
  Support = -> [XY_Plane018]
  sketch-geometry (4):
    g0: LineSegment StartX=-7 StartY=7 StartZ=0 EndX=7 EndY=7 EndZ=0
    g1: LineSegment StartX=7 StartY=7 StartZ=0 EndX=7 EndY=-7 EndZ=0
    g2: LineSegment StartX=7 StartY=-7 StartZ=0 EndX=-7 EndY=-7 EndZ=0
    g3: LineSegment StartX=-7 StartY=-7 StartZ=0 EndX=-7 EndY=7 EndZ=0
  constraints (8):
    c: Coincident(g0,g1)
    c: Coincident(g1,g2)
    c: Coincident(g2,g3)
    c: Coincident(g3,g0)
    c: Horizontal(g0)
    c: Horizontal(g2)
    c: Vertical(g1)
    c: Vertical(g3)
FEATURE [PartDesign::Pad] Pad064
  Length = 9
  Length2 = 100
  Profile = -> Sketch103
  Type = 0
FEATURE [PartDesign::Body] Body018  label="Joystick_under"
  Group = -> [Sketch103,Pad064]
  Origin = -> Origin018
  Tip = -> Pad064
